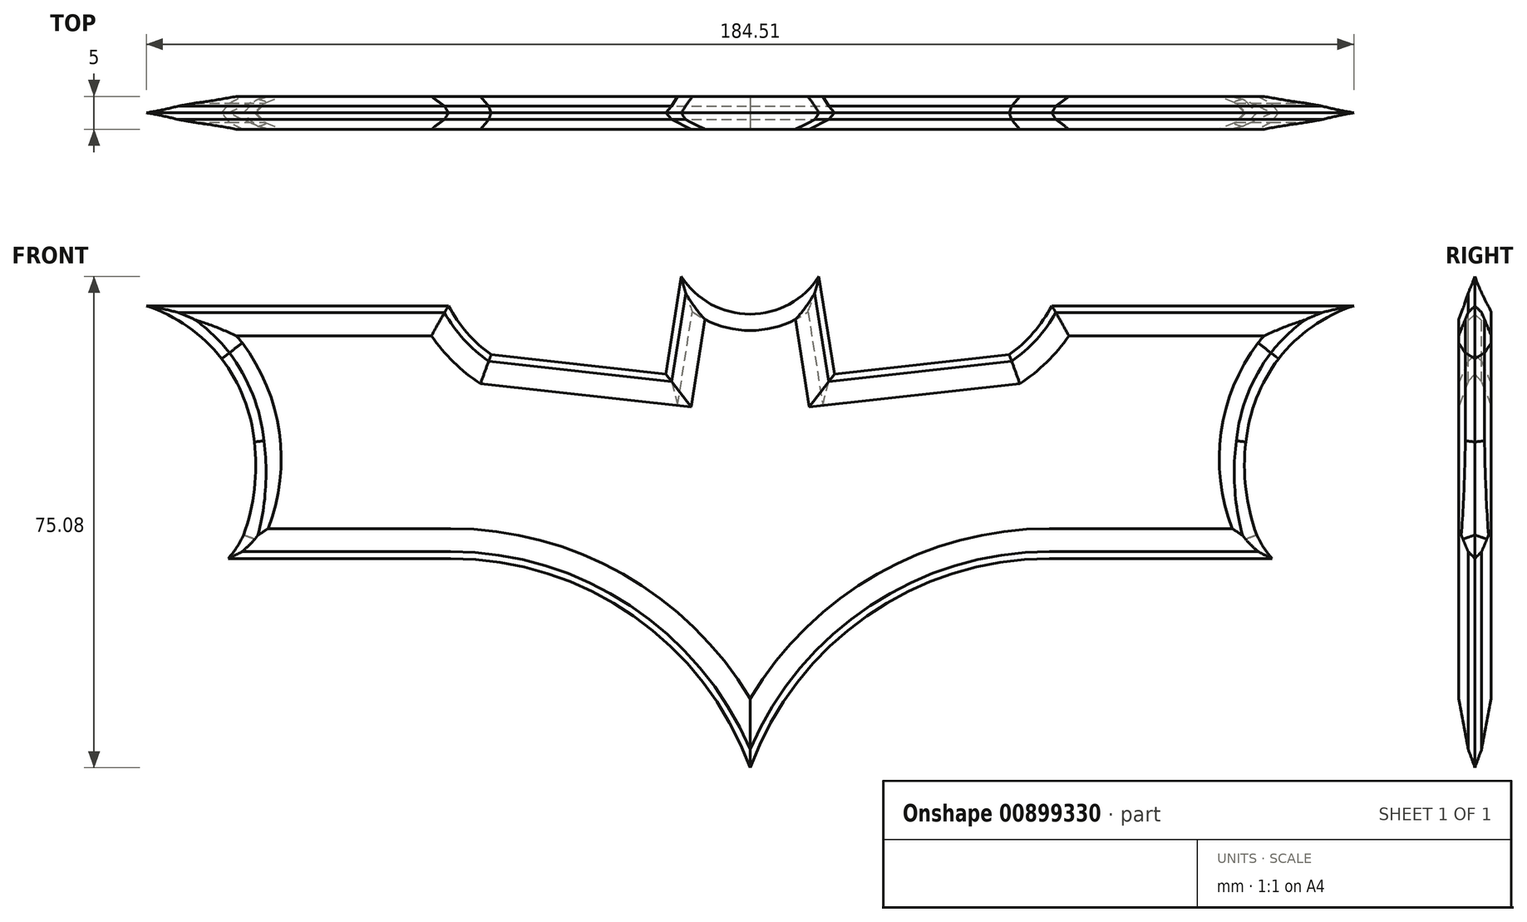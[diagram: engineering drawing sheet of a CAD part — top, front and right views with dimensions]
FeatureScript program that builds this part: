
annotation { "Feature Type Name" : "Feature", "Feature Type Description" : "" }
export const myFeature = defineFeature(function(context is Context, id is Id, definition is map)
    precondition{}
    {
        {
            var Q0;
            Q0=qCreatedBy(makeId("Front.planeOp"),FACE);
            var sketch = newSketch(context, id + "F0", { "sketchPlane" : qUnion([Q0])});
            skLineSegment(sketch, "E0", {"start": v(0, 0) * mm, "end": v(50, 0) * mm});
            skLineSegment(sketch, "E1", {"start": v(57, -8.48) * mm, "end": v(86.82, -11.78) * mm});
            skPoint(sketch, "E2", {"position": v(84.15, -2.31) * mm});
            skLineSegment(sketch, "E3", {"start": v(96.59, 0.22) * mm, "end": v(96.59, 7.53) * mm});
            skArc(sketch, "E4", {"start": v(86.82, 8.22) * mm, "mid": v(96.59, 0.22) * mm, "end": v(106.35, 8.22) * mm});
            skArc(sketch, "E5", {"start": v(96.59, -74.78) * mm, "mid": v(79.39, -50.1) * mm, "end": v(50.84, -40.6) * mm});
            skArc(sketch, "E6", {"start": v(15.84, -9.08) * mm, "mid": v(8.8, -3) * mm, "end": v(0, 0) * mm});
            skArc(sketch, "E7", {"start": v(20.83, -21.8) * mm, "mid": v(19.2, -15.1) * mm, "end": v(15.84, -9.08) * mm});
            skArc(sketch, "E8", {"start": v(19.17, -36.02) * mm, "mid": v(20.84, -29) * mm, "end": v(20.83, -21.8) * mm});
            skArc(sketch, "E9", {"start": v(15.84, -40.6) * mm, "mid": v(17.74, -38.48) * mm, "end": v(19.17, -36.02) * mm});
            skLineSegment(sketch, "E10", {"start": v(15.84, -40.6) * mm, "end": v(50.84, -40.6) * mm});
            skArc(sketch, "E11.MirrorCS", {"start": v(177.33, -9.08) * mm, "mid": v(184.37, -3) * mm, "end": v(193.17, 0) * mm});
            skArc(sketch, "E12.MirrorCS", {"start": v(172.34, -21.8) * mm, "mid": v(173.97, -15.1) * mm, "end": v(177.33, -9.08) * mm});
            skLineSegment(sketch, "E13.MirrorCS", {"start": v(193.17, 0) * mm, "end": v(143.17, 0) * mm});
            skLineSegment(sketch, "E14.MirrorCS", {"start": v(136.17, -8.48) * mm, "end": v(106.35, -11.78) * mm});
            skArc(sketch, "E15.MirrorCS", {"start": v(174, -36.02) * mm, "mid": v(172.33, -29) * mm, "end": v(172.34, -21.8) * mm});
            skArc(sketch, "E16.MirrorCS", {"start": v(177.33, -40.6) * mm, "mid": v(175.43, -38.48) * mm, "end": v(174, -36.02) * mm});
            skLineSegment(sketch, "E17.MirrorCS", {"start": v(177.33, -40.6) * mm, "end": v(142.33, -40.6) * mm});
            skArc(sketch, "E18.MirrorCS", {"start": v(96.59, -74.78) * mm, "mid": v(113.78, -50.1) * mm, "end": v(142.33, -40.6) * mm});
            skArc(sketch, "E19", {"start": v(50, 0) * mm, "mid": v(52.95, -4.7) * mm, "end": v(57, -8.48) * mm});
            skArc(sketch, "E20.MirrorCS", {"start": v(143.17, 0) * mm, "mid": v(140.23, -4.7) * mm, "end": v(136.17, -8.48) * mm});
            skLineSegment(sketch, "E21", {"start": v(86.82, 8.22) * mm, "end": v(83.72, -11.43) * mm});
            skLineSegment(sketch, "E22.MirrorCS", {"start": v(106.35, 8.22) * mm, "end": v(109.46, -11.43) * mm});
            skSolve(sketch);
        }
        {
            var Q0;
            Q0 = qSketchRegion(id + "F0", true);
            extrude(context, id + "F1", {"entities" : qUnion([Q0]), "depth" : 5 * mm, "offsetDistance" : 25 * mm});
        }
        {
            var Q0;
            Q0=makeQuery(id+"F1.opExtrude","CAP_EDGE",EDGE,{"disambiguationData":[OSD([sQuery(id+"F0.wireOp",EDGE,"E0")])],"isStart":false});
            var Q1;
            Q1=makeQuery(id+"F1.opExtrude","CAP_EDGE",EDGE,{"disambiguationData":[OSD([sQuery(id+"F0.wireOp",EDGE,"E0")])],"isStart":true});
            var Q2;
            Q2=makeQuery(id+"F1.opExtrude","CAP_EDGE",EDGE,{"disambiguationData":[OSD([sQuery(id+"F0.wireOp",EDGE,"E10")])],"isStart":false});
            var Q3;
            Q3=makeQuery(id+"F1.opExtrude","CAP_EDGE",EDGE,{"disambiguationData":[OSD([sQuery(id+"F0.wireOp",EDGE,"E10")])],"isStart":true});
            chamfer(context, id + "F2", {"entities" : qUnion([Q0, Q1, Q2, Q3]), "width" : 3.5 * mm, "tangentPropagation" : true});
        }
        {
            var Q0;
            Q0=makeQuery(id+"F1.opExtrude","CAP_EDGE",EDGE,{"disambiguationData":[OSD([sQuery(id+"F0.wireOp",EDGE,"E19")])],"isStart":false});
            var Q1;
            Q1=makeQuery(id+"F1.opExtrude","CAP_EDGE",EDGE,{"disambiguationData":[OSD([sQuery(id+"F0.wireOp",EDGE,"E19")])],"isStart":true});
            chamfer(context, id + "F3", {"entities" : qUnion([Q0, Q1]), "width" : 2.5 * mm, "tangentPropagation" : true});
        }
        {
            var Q0;
            Q0=makeQuery(id+"F1.opExtrude","CAP_EDGE",EDGE,{"disambiguationData":[OSD([sQuery(id+"F0.wireOp",EDGE,"E1")])],"isStart":false});
            var Q1;
            Q1=makeQuery(id+"F1.opExtrude","CAP_EDGE",EDGE,{"disambiguationData":[OSD([sQuery(id+"F0.wireOp",EDGE,"E1")])],"isStart":true});
            chamfer(context, id + "F4", {"entities" : qUnion([Q0, Q1]), "width" : 2.5 * mm, "tangentPropagation" : true});
        }
        {
            var Q0;
            Q0=makeQuery(id+"F1.opExtrude","CAP_EDGE",EDGE,{"disambiguationData":[OSD([sQuery(id+"F0.wireOp",EDGE,"E13.MirrorCS")])],"isStart":false});
            var Q1;
            Q1=makeQuery(id+"F1.opExtrude","CAP_EDGE",EDGE,{"disambiguationData":[OSD([sQuery(id+"F0.wireOp",EDGE,"E13.MirrorCS")])],"isStart":true});
            var Q2;
            Q2=makeQuery(id+"F1.opExtrude","CAP_EDGE",EDGE,{"disambiguationData":[OSD([sQuery(id+"F0.wireOp",EDGE,"E17.MirrorCS")])],"isStart":false});
            var Q3;
            Q3=makeQuery(id+"F1.opExtrude","CAP_EDGE",EDGE,{"disambiguationData":[OSD([sQuery(id+"F0.wireOp",EDGE,"E17.MirrorCS")])],"isStart":true});
            chamfer(context, id + "F5", {"entities" : qUnion([Q0, Q1, Q2, Q3]), "width" : 3.5 * mm, "tangentPropagation" : true});
        }
        {
            var Q0;
            Q0=makeQuery(id+"F1.opExtrude","CAP_EDGE",EDGE,{"disambiguationData":[OSD([sQuery(id+"F0.wireOp",EDGE,"E20.MirrorCS")])],"isStart":true});
            var Q1;
            Q1=makeQuery(id+"F1.opExtrude","CAP_EDGE",EDGE,{"disambiguationData":[OSD([sQuery(id+"F0.wireOp",EDGE,"E20.MirrorCS")])],"isStart":false});
            var Q2;
            Q2=makeQuery(id+"F1.opExtrude","CAP_EDGE",EDGE,{"disambiguationData":[OSD([sQuery(id+"F0.wireOp",EDGE,"E14.MirrorCS")])],"isStart":true});
            var Q3;
            Q3=makeQuery(id+"F1.opExtrude","CAP_EDGE",EDGE,{"disambiguationData":[OSD([sQuery(id+"F0.wireOp",EDGE,"E14.MirrorCS")])],"isStart":false});
            var Q4;
            Q4=makeQuery(id+"F1.opExtrude","CAP_EDGE",EDGE,{"disambiguationData":[OSD([sQuery(id+"F0.wireOp",EDGE,"E22.MirrorCS")])],"isStart":true});
            var Q5;
            Q5=makeQuery(id+"F1.opExtrude","CAP_EDGE",EDGE,{"disambiguationData":[OSD([sQuery(id+"F0.wireOp",EDGE,"E22.MirrorCS")])],"isStart":false});
            var Q6;
            Q6=makeQuery(id+"F1.opExtrude","CAP_EDGE",EDGE,{"disambiguationData":[OSD([sQuery(id+"F0.wireOp",EDGE,"E21")])],"isStart":true});
            var Q7;
            Q7=makeQuery(id+"F1.opExtrude","CAP_EDGE",EDGE,{"disambiguationData":[OSD([sQuery(id+"F0.wireOp",EDGE,"E21")])],"isStart":false});
            chamfer(context, id + "F6", {"entities" : qUnion([Q0, Q1, Q2, Q3, Q4, Q5, Q6, Q7]), "width" : 2.5 * mm, "tangentPropagation" : true});
        }
        {
            var Q0;
            Q0=makeQuery(id+"F1.opExtrude","CAP_EDGE",EDGE,{"disambiguationData":[OSD([sQuery(id+"F0.wireOp",EDGE,"E4")])],"isStart":true});
            var Q1;
            Q1=makeQuery(id+"F1.opExtrude","CAP_EDGE",EDGE,{"disambiguationData":[OSD([sQuery(id+"F0.wireOp",EDGE,"E4")])],"isStart":false});
            chamfer(context, id + "F7", {"entities" : qUnion([Q0, Q1]), "width" : 5 * mm, "tangentPropagation" : true});
        }
        {
            var Q0;
            {var subQ0=sQuery(id+"F0.wireOp",EDGE,"E13.MirrorCS");Q0=makeQuery(id+"F5.opChamfer","BLEND_EDGE",EDGE,{"blendedFrom":[makeQuery(id+"F1.opExtrude","CAP_EDGE",EDGE,{"disambiguationData":[OSD([subQ0])],"isStart":true}),makeQuery(id+"F1.opExtrude","CAP_FACE",FACE,{"disambiguationData":[OSD([sQuery(id+"F0.wireOp",EDGE,"E0"),sQuery(id+"F0.wireOp",EDGE,"E1"),sQuery(id+"F0.wireOp",EDGE,"E4"),sQuery(id+"F0.wireOp",EDGE,"E5"),sQuery(id+"F0.wireOp",EDGE,"E6"),sQuery(id+"F0.wireOp",EDGE,"E7"),sQuery(id+"F0.wireOp",EDGE,"E8"),sQuery(id+"F0.wireOp",EDGE,"E9"),sQuery(id+"F0.wireOp",EDGE,"E10"),sQuery(id+"F0.wireOp",EDGE,"E11.MirrorCS"),sQuery(id+"F0.wireOp",EDGE,"E12.MirrorCS"),subQ0,sQuery(id+"F0.wireOp",EDGE,"E14.MirrorCS"),sQuery(id+"F0.wireOp",EDGE,"E15.MirrorCS"),sQuery(id+"F0.wireOp",EDGE,"E16.MirrorCS"),sQuery(id+"F0.wireOp",EDGE,"E17.MirrorCS"),sQuery(id+"F0.wireOp",EDGE,"E18.MirrorCS"),sQuery(id+"F0.wireOp",EDGE,"E19"),sQuery(id+"F0.wireOp",EDGE,"E20.MirrorCS"),sQuery(id+"F0.wireOp",EDGE,"E21"),sQuery(id+"F0.wireOp",EDGE,"E22.MirrorCS")])],"isStart":true})],"blendedInto":[makeQuery(id+"F1.opExtrude","CAP_FACE",FACE,{"disambiguationData":[OSD([sQuery(id+"F0.wireOp",EDGE,"E0"),sQuery(id+"F0.wireOp",EDGE,"E1"),sQuery(id+"F0.wireOp",EDGE,"E4"),sQuery(id+"F0.wireOp",EDGE,"E5"),sQuery(id+"F0.wireOp",EDGE,"E6"),sQuery(id+"F0.wireOp",EDGE,"E7"),sQuery(id+"F0.wireOp",EDGE,"E8"),sQuery(id+"F0.wireOp",EDGE,"E9"),sQuery(id+"F0.wireOp",EDGE,"E10"),sQuery(id+"F0.wireOp",EDGE,"E11.MirrorCS"),sQuery(id+"F0.wireOp",EDGE,"E12.MirrorCS"),subQ0,sQuery(id+"F0.wireOp",EDGE,"E14.MirrorCS"),sQuery(id+"F0.wireOp",EDGE,"E15.MirrorCS"),sQuery(id+"F0.wireOp",EDGE,"E16.MirrorCS"),sQuery(id+"F0.wireOp",EDGE,"E17.MirrorCS"),sQuery(id+"F0.wireOp",EDGE,"E18.MirrorCS"),sQuery(id+"F0.wireOp",EDGE,"E19"),sQuery(id+"F0.wireOp",EDGE,"E20.MirrorCS"),sQuery(id+"F0.wireOp",EDGE,"E21"),sQuery(id+"F0.wireOp",EDGE,"E22.MirrorCS")])],"isStart":true})]});}
            var Q1;
            {var subQ0=sQuery(id+"F0.wireOp",EDGE,"E12.MirrorCS");Q1=makeQuery(id+"F5.opChamfer","BLEND_EDGE",EDGE,{"blendedFrom":[makeQuery(id+"F1.opExtrude","CAP_EDGE",EDGE,{"disambiguationData":[OSD([subQ0])],"isStart":true}),makeQuery(id+"F1.opExtrude","CAP_FACE",FACE,{"disambiguationData":[OSD([sQuery(id+"F0.wireOp",EDGE,"E0"),sQuery(id+"F0.wireOp",EDGE,"E1"),sQuery(id+"F0.wireOp",EDGE,"E4"),sQuery(id+"F0.wireOp",EDGE,"E5"),sQuery(id+"F0.wireOp",EDGE,"E6"),sQuery(id+"F0.wireOp",EDGE,"E7"),sQuery(id+"F0.wireOp",EDGE,"E8"),sQuery(id+"F0.wireOp",EDGE,"E9"),sQuery(id+"F0.wireOp",EDGE,"E10"),sQuery(id+"F0.wireOp",EDGE,"E11.MirrorCS"),subQ0,sQuery(id+"F0.wireOp",EDGE,"E13.MirrorCS"),sQuery(id+"F0.wireOp",EDGE,"E14.MirrorCS"),sQuery(id+"F0.wireOp",EDGE,"E15.MirrorCS"),sQuery(id+"F0.wireOp",EDGE,"E16.MirrorCS"),sQuery(id+"F0.wireOp",EDGE,"E17.MirrorCS"),sQuery(id+"F0.wireOp",EDGE,"E18.MirrorCS"),sQuery(id+"F0.wireOp",EDGE,"E19"),sQuery(id+"F0.wireOp",EDGE,"E20.MirrorCS"),sQuery(id+"F0.wireOp",EDGE,"E21"),sQuery(id+"F0.wireOp",EDGE,"E22.MirrorCS")])],"isStart":true})],"blendedInto":[makeQuery(id+"F1.opExtrude","CAP_FACE",FACE,{"disambiguationData":[OSD([sQuery(id+"F0.wireOp",EDGE,"E0"),sQuery(id+"F0.wireOp",EDGE,"E1"),sQuery(id+"F0.wireOp",EDGE,"E4"),sQuery(id+"F0.wireOp",EDGE,"E5"),sQuery(id+"F0.wireOp",EDGE,"E6"),sQuery(id+"F0.wireOp",EDGE,"E7"),sQuery(id+"F0.wireOp",EDGE,"E8"),sQuery(id+"F0.wireOp",EDGE,"E9"),sQuery(id+"F0.wireOp",EDGE,"E10"),sQuery(id+"F0.wireOp",EDGE,"E11.MirrorCS"),subQ0,sQuery(id+"F0.wireOp",EDGE,"E13.MirrorCS"),sQuery(id+"F0.wireOp",EDGE,"E14.MirrorCS"),sQuery(id+"F0.wireOp",EDGE,"E15.MirrorCS"),sQuery(id+"F0.wireOp",EDGE,"E16.MirrorCS"),sQuery(id+"F0.wireOp",EDGE,"E17.MirrorCS"),sQuery(id+"F0.wireOp",EDGE,"E18.MirrorCS"),sQuery(id+"F0.wireOp",EDGE,"E19"),sQuery(id+"F0.wireOp",EDGE,"E20.MirrorCS"),sQuery(id+"F0.wireOp",EDGE,"E21"),sQuery(id+"F0.wireOp",EDGE,"E22.MirrorCS")])],"isStart":true})]});}
            var Q2;
            {var subQ0=sQuery(id+"F0.wireOp",EDGE,"E14.MirrorCS");Q2=makeQuery(id+"F6.opChamfer","BLEND_EDGE",EDGE,{"blendedFrom":[makeQuery(id+"F1.opExtrude","CAP_EDGE",EDGE,{"disambiguationData":[OSD([subQ0])],"isStart":true}),makeQuery(id+"F1.opExtrude","CAP_FACE",FACE,{"disambiguationData":[OSD([sQuery(id+"F0.wireOp",EDGE,"E0"),sQuery(id+"F0.wireOp",EDGE,"E1"),sQuery(id+"F0.wireOp",EDGE,"E4"),sQuery(id+"F0.wireOp",EDGE,"E5"),sQuery(id+"F0.wireOp",EDGE,"E6"),sQuery(id+"F0.wireOp",EDGE,"E7"),sQuery(id+"F0.wireOp",EDGE,"E8"),sQuery(id+"F0.wireOp",EDGE,"E9"),sQuery(id+"F0.wireOp",EDGE,"E10"),sQuery(id+"F0.wireOp",EDGE,"E11.MirrorCS"),sQuery(id+"F0.wireOp",EDGE,"E12.MirrorCS"),sQuery(id+"F0.wireOp",EDGE,"E13.MirrorCS"),subQ0,sQuery(id+"F0.wireOp",EDGE,"E15.MirrorCS"),sQuery(id+"F0.wireOp",EDGE,"E16.MirrorCS"),sQuery(id+"F0.wireOp",EDGE,"E17.MirrorCS"),sQuery(id+"F0.wireOp",EDGE,"E18.MirrorCS"),sQuery(id+"F0.wireOp",EDGE,"E19"),sQuery(id+"F0.wireOp",EDGE,"E20.MirrorCS"),sQuery(id+"F0.wireOp",EDGE,"E21"),sQuery(id+"F0.wireOp",EDGE,"E22.MirrorCS")])],"isStart":true})],"blendedInto":[makeQuery(id+"F1.opExtrude","CAP_FACE",FACE,{"disambiguationData":[OSD([sQuery(id+"F0.wireOp",EDGE,"E0"),sQuery(id+"F0.wireOp",EDGE,"E1"),sQuery(id+"F0.wireOp",EDGE,"E4"),sQuery(id+"F0.wireOp",EDGE,"E5"),sQuery(id+"F0.wireOp",EDGE,"E6"),sQuery(id+"F0.wireOp",EDGE,"E7"),sQuery(id+"F0.wireOp",EDGE,"E8"),sQuery(id+"F0.wireOp",EDGE,"E9"),sQuery(id+"F0.wireOp",EDGE,"E10"),sQuery(id+"F0.wireOp",EDGE,"E11.MirrorCS"),sQuery(id+"F0.wireOp",EDGE,"E12.MirrorCS"),sQuery(id+"F0.wireOp",EDGE,"E13.MirrorCS"),subQ0,sQuery(id+"F0.wireOp",EDGE,"E15.MirrorCS"),sQuery(id+"F0.wireOp",EDGE,"E16.MirrorCS"),sQuery(id+"F0.wireOp",EDGE,"E17.MirrorCS"),sQuery(id+"F0.wireOp",EDGE,"E18.MirrorCS"),sQuery(id+"F0.wireOp",EDGE,"E19"),sQuery(id+"F0.wireOp",EDGE,"E20.MirrorCS"),sQuery(id+"F0.wireOp",EDGE,"E21"),sQuery(id+"F0.wireOp",EDGE,"E22.MirrorCS")])],"isStart":true})]});}
            var Q3;
            {var subQ0=sQuery(id+"F0.wireOp",EDGE,"E17.MirrorCS");Q3=makeQuery(id+"F5.opChamfer","BLEND_EDGE",EDGE,{"blendedFrom":[makeQuery(id+"F1.opExtrude","CAP_EDGE",EDGE,{"disambiguationData":[OSD([subQ0])],"isStart":true}),makeQuery(id+"F1.opExtrude","CAP_FACE",FACE,{"disambiguationData":[OSD([sQuery(id+"F0.wireOp",EDGE,"E0"),sQuery(id+"F0.wireOp",EDGE,"E1"),sQuery(id+"F0.wireOp",EDGE,"E4"),sQuery(id+"F0.wireOp",EDGE,"E5"),sQuery(id+"F0.wireOp",EDGE,"E6"),sQuery(id+"F0.wireOp",EDGE,"E7"),sQuery(id+"F0.wireOp",EDGE,"E8"),sQuery(id+"F0.wireOp",EDGE,"E9"),sQuery(id+"F0.wireOp",EDGE,"E10"),sQuery(id+"F0.wireOp",EDGE,"E11.MirrorCS"),sQuery(id+"F0.wireOp",EDGE,"E12.MirrorCS"),sQuery(id+"F0.wireOp",EDGE,"E13.MirrorCS"),sQuery(id+"F0.wireOp",EDGE,"E14.MirrorCS"),sQuery(id+"F0.wireOp",EDGE,"E15.MirrorCS"),sQuery(id+"F0.wireOp",EDGE,"E16.MirrorCS"),subQ0,sQuery(id+"F0.wireOp",EDGE,"E18.MirrorCS"),sQuery(id+"F0.wireOp",EDGE,"E19"),sQuery(id+"F0.wireOp",EDGE,"E20.MirrorCS"),sQuery(id+"F0.wireOp",EDGE,"E21"),sQuery(id+"F0.wireOp",EDGE,"E22.MirrorCS")])],"isStart":true})],"blendedInto":[makeQuery(id+"F1.opExtrude","CAP_FACE",FACE,{"disambiguationData":[OSD([sQuery(id+"F0.wireOp",EDGE,"E0"),sQuery(id+"F0.wireOp",EDGE,"E1"),sQuery(id+"F0.wireOp",EDGE,"E4"),sQuery(id+"F0.wireOp",EDGE,"E5"),sQuery(id+"F0.wireOp",EDGE,"E6"),sQuery(id+"F0.wireOp",EDGE,"E7"),sQuery(id+"F0.wireOp",EDGE,"E8"),sQuery(id+"F0.wireOp",EDGE,"E9"),sQuery(id+"F0.wireOp",EDGE,"E10"),sQuery(id+"F0.wireOp",EDGE,"E11.MirrorCS"),sQuery(id+"F0.wireOp",EDGE,"E12.MirrorCS"),sQuery(id+"F0.wireOp",EDGE,"E13.MirrorCS"),sQuery(id+"F0.wireOp",EDGE,"E14.MirrorCS"),sQuery(id+"F0.wireOp",EDGE,"E15.MirrorCS"),sQuery(id+"F0.wireOp",EDGE,"E16.MirrorCS"),subQ0,sQuery(id+"F0.wireOp",EDGE,"E18.MirrorCS"),sQuery(id+"F0.wireOp",EDGE,"E19"),sQuery(id+"F0.wireOp",EDGE,"E20.MirrorCS"),sQuery(id+"F0.wireOp",EDGE,"E21"),sQuery(id+"F0.wireOp",EDGE,"E22.MirrorCS")])],"isStart":true})]});}
            var Q4;
            {var subQ0=sQuery(id+"F0.wireOp",EDGE,"E1");Q4=makeQuery(id+"F4.opChamfer","BLEND_EDGE",EDGE,{"blendedFrom":[makeQuery(id+"F1.opExtrude","CAP_EDGE",EDGE,{"disambiguationData":[OSD([subQ0])],"isStart":true}),makeQuery(id+"F1.opExtrude","CAP_FACE",FACE,{"disambiguationData":[OSD([sQuery(id+"F0.wireOp",EDGE,"E0"),subQ0,sQuery(id+"F0.wireOp",EDGE,"E4"),sQuery(id+"F0.wireOp",EDGE,"E5"),sQuery(id+"F0.wireOp",EDGE,"E6"),sQuery(id+"F0.wireOp",EDGE,"E7"),sQuery(id+"F0.wireOp",EDGE,"E8"),sQuery(id+"F0.wireOp",EDGE,"E9"),sQuery(id+"F0.wireOp",EDGE,"E10"),sQuery(id+"F0.wireOp",EDGE,"E11.MirrorCS"),sQuery(id+"F0.wireOp",EDGE,"E12.MirrorCS"),sQuery(id+"F0.wireOp",EDGE,"E13.MirrorCS"),sQuery(id+"F0.wireOp",EDGE,"E14.MirrorCS"),sQuery(id+"F0.wireOp",EDGE,"E15.MirrorCS"),sQuery(id+"F0.wireOp",EDGE,"E16.MirrorCS"),sQuery(id+"F0.wireOp",EDGE,"E17.MirrorCS"),sQuery(id+"F0.wireOp",EDGE,"E18.MirrorCS"),sQuery(id+"F0.wireOp",EDGE,"E19"),sQuery(id+"F0.wireOp",EDGE,"E20.MirrorCS"),sQuery(id+"F0.wireOp",EDGE,"E21"),sQuery(id+"F0.wireOp",EDGE,"E22.MirrorCS")])],"isStart":true})],"blendedInto":[makeQuery(id+"F1.opExtrude","CAP_FACE",FACE,{"disambiguationData":[OSD([sQuery(id+"F0.wireOp",EDGE,"E0"),subQ0,sQuery(id+"F0.wireOp",EDGE,"E4"),sQuery(id+"F0.wireOp",EDGE,"E5"),sQuery(id+"F0.wireOp",EDGE,"E6"),sQuery(id+"F0.wireOp",EDGE,"E7"),sQuery(id+"F0.wireOp",EDGE,"E8"),sQuery(id+"F0.wireOp",EDGE,"E9"),sQuery(id+"F0.wireOp",EDGE,"E10"),sQuery(id+"F0.wireOp",EDGE,"E11.MirrorCS"),sQuery(id+"F0.wireOp",EDGE,"E12.MirrorCS"),sQuery(id+"F0.wireOp",EDGE,"E13.MirrorCS"),sQuery(id+"F0.wireOp",EDGE,"E14.MirrorCS"),sQuery(id+"F0.wireOp",EDGE,"E15.MirrorCS"),sQuery(id+"F0.wireOp",EDGE,"E16.MirrorCS"),sQuery(id+"F0.wireOp",EDGE,"E17.MirrorCS"),sQuery(id+"F0.wireOp",EDGE,"E18.MirrorCS"),sQuery(id+"F0.wireOp",EDGE,"E19"),sQuery(id+"F0.wireOp",EDGE,"E20.MirrorCS"),sQuery(id+"F0.wireOp",EDGE,"E21"),sQuery(id+"F0.wireOp",EDGE,"E22.MirrorCS")])],"isStart":true})]});}
            var Q5;
            {var subQ0=sQuery(id+"F0.wireOp",EDGE,"E0");Q5=makeQuery(id+"F2.opChamfer","BLEND_EDGE",EDGE,{"blendedFrom":[makeQuery(id+"F1.opExtrude","CAP_EDGE",EDGE,{"disambiguationData":[OSD([subQ0])],"isStart":true}),makeQuery(id+"F1.opExtrude","CAP_FACE",FACE,{"disambiguationData":[OSD([subQ0,sQuery(id+"F0.wireOp",EDGE,"E1"),sQuery(id+"F0.wireOp",EDGE,"E4"),sQuery(id+"F0.wireOp",EDGE,"E5"),sQuery(id+"F0.wireOp",EDGE,"E6"),sQuery(id+"F0.wireOp",EDGE,"E7"),sQuery(id+"F0.wireOp",EDGE,"E8"),sQuery(id+"F0.wireOp",EDGE,"E9"),sQuery(id+"F0.wireOp",EDGE,"E10"),sQuery(id+"F0.wireOp",EDGE,"E11.MirrorCS"),sQuery(id+"F0.wireOp",EDGE,"E12.MirrorCS"),sQuery(id+"F0.wireOp",EDGE,"E13.MirrorCS"),sQuery(id+"F0.wireOp",EDGE,"E14.MirrorCS"),sQuery(id+"F0.wireOp",EDGE,"E15.MirrorCS"),sQuery(id+"F0.wireOp",EDGE,"E16.MirrorCS"),sQuery(id+"F0.wireOp",EDGE,"E17.MirrorCS"),sQuery(id+"F0.wireOp",EDGE,"E18.MirrorCS"),sQuery(id+"F0.wireOp",EDGE,"E19"),sQuery(id+"F0.wireOp",EDGE,"E20.MirrorCS"),sQuery(id+"F0.wireOp",EDGE,"E21"),sQuery(id+"F0.wireOp",EDGE,"E22.MirrorCS")])],"isStart":true})],"blendedInto":[makeQuery(id+"F1.opExtrude","CAP_FACE",FACE,{"disambiguationData":[OSD([subQ0,sQuery(id+"F0.wireOp",EDGE,"E1"),sQuery(id+"F0.wireOp",EDGE,"E4"),sQuery(id+"F0.wireOp",EDGE,"E5"),sQuery(id+"F0.wireOp",EDGE,"E6"),sQuery(id+"F0.wireOp",EDGE,"E7"),sQuery(id+"F0.wireOp",EDGE,"E8"),sQuery(id+"F0.wireOp",EDGE,"E9"),sQuery(id+"F0.wireOp",EDGE,"E10"),sQuery(id+"F0.wireOp",EDGE,"E11.MirrorCS"),sQuery(id+"F0.wireOp",EDGE,"E12.MirrorCS"),sQuery(id+"F0.wireOp",EDGE,"E13.MirrorCS"),sQuery(id+"F0.wireOp",EDGE,"E14.MirrorCS"),sQuery(id+"F0.wireOp",EDGE,"E15.MirrorCS"),sQuery(id+"F0.wireOp",EDGE,"E16.MirrorCS"),sQuery(id+"F0.wireOp",EDGE,"E17.MirrorCS"),sQuery(id+"F0.wireOp",EDGE,"E18.MirrorCS"),sQuery(id+"F0.wireOp",EDGE,"E19"),sQuery(id+"F0.wireOp",EDGE,"E20.MirrorCS"),sQuery(id+"F0.wireOp",EDGE,"E21"),sQuery(id+"F0.wireOp",EDGE,"E22.MirrorCS")])],"isStart":true})]});}
            var Q6;
            {var subQ0=sQuery(id+"F0.wireOp",EDGE,"E20.MirrorCS");Q6=makeQuery(id+"F6.opChamfer","BLEND_EDGE",EDGE,{"blendedFrom":[makeQuery(id+"F1.opExtrude","CAP_EDGE",EDGE,{"disambiguationData":[OSD([subQ0])],"isStart":true}),makeQuery(id+"F1.opExtrude","CAP_FACE",FACE,{"disambiguationData":[OSD([sQuery(id+"F0.wireOp",EDGE,"E0"),sQuery(id+"F0.wireOp",EDGE,"E1"),sQuery(id+"F0.wireOp",EDGE,"E4"),sQuery(id+"F0.wireOp",EDGE,"E5"),sQuery(id+"F0.wireOp",EDGE,"E6"),sQuery(id+"F0.wireOp",EDGE,"E7"),sQuery(id+"F0.wireOp",EDGE,"E8"),sQuery(id+"F0.wireOp",EDGE,"E9"),sQuery(id+"F0.wireOp",EDGE,"E10"),sQuery(id+"F0.wireOp",EDGE,"E11.MirrorCS"),sQuery(id+"F0.wireOp",EDGE,"E12.MirrorCS"),sQuery(id+"F0.wireOp",EDGE,"E13.MirrorCS"),sQuery(id+"F0.wireOp",EDGE,"E14.MirrorCS"),sQuery(id+"F0.wireOp",EDGE,"E15.MirrorCS"),sQuery(id+"F0.wireOp",EDGE,"E16.MirrorCS"),sQuery(id+"F0.wireOp",EDGE,"E17.MirrorCS"),sQuery(id+"F0.wireOp",EDGE,"E18.MirrorCS"),sQuery(id+"F0.wireOp",EDGE,"E19"),subQ0,sQuery(id+"F0.wireOp",EDGE,"E21"),sQuery(id+"F0.wireOp",EDGE,"E22.MirrorCS")])],"isStart":true})],"blendedInto":[makeQuery(id+"F1.opExtrude","CAP_FACE",FACE,{"disambiguationData":[OSD([sQuery(id+"F0.wireOp",EDGE,"E0"),sQuery(id+"F0.wireOp",EDGE,"E1"),sQuery(id+"F0.wireOp",EDGE,"E4"),sQuery(id+"F0.wireOp",EDGE,"E5"),sQuery(id+"F0.wireOp",EDGE,"E6"),sQuery(id+"F0.wireOp",EDGE,"E7"),sQuery(id+"F0.wireOp",EDGE,"E8"),sQuery(id+"F0.wireOp",EDGE,"E9"),sQuery(id+"F0.wireOp",EDGE,"E10"),sQuery(id+"F0.wireOp",EDGE,"E11.MirrorCS"),sQuery(id+"F0.wireOp",EDGE,"E12.MirrorCS"),sQuery(id+"F0.wireOp",EDGE,"E13.MirrorCS"),sQuery(id+"F0.wireOp",EDGE,"E14.MirrorCS"),sQuery(id+"F0.wireOp",EDGE,"E15.MirrorCS"),sQuery(id+"F0.wireOp",EDGE,"E16.MirrorCS"),sQuery(id+"F0.wireOp",EDGE,"E17.MirrorCS"),sQuery(id+"F0.wireOp",EDGE,"E18.MirrorCS"),sQuery(id+"F0.wireOp",EDGE,"E19"),subQ0,sQuery(id+"F0.wireOp",EDGE,"E21"),sQuery(id+"F0.wireOp",EDGE,"E22.MirrorCS")])],"isStart":true})]});}
            var Q7;
            {var subQ0=sQuery(id+"F0.wireOp",EDGE,"E19");Q7=makeQuery(id+"F3.opChamfer","BLEND_EDGE",EDGE,{"blendedFrom":[makeQuery(id+"F1.opExtrude","CAP_EDGE",EDGE,{"disambiguationData":[OSD([subQ0])],"isStart":true}),makeQuery(id+"F1.opExtrude","CAP_FACE",FACE,{"disambiguationData":[OSD([sQuery(id+"F0.wireOp",EDGE,"E0"),sQuery(id+"F0.wireOp",EDGE,"E1"),sQuery(id+"F0.wireOp",EDGE,"E4"),sQuery(id+"F0.wireOp",EDGE,"E5"),sQuery(id+"F0.wireOp",EDGE,"E6"),sQuery(id+"F0.wireOp",EDGE,"E7"),sQuery(id+"F0.wireOp",EDGE,"E8"),sQuery(id+"F0.wireOp",EDGE,"E9"),sQuery(id+"F0.wireOp",EDGE,"E10"),sQuery(id+"F0.wireOp",EDGE,"E11.MirrorCS"),sQuery(id+"F0.wireOp",EDGE,"E12.MirrorCS"),sQuery(id+"F0.wireOp",EDGE,"E13.MirrorCS"),sQuery(id+"F0.wireOp",EDGE,"E14.MirrorCS"),sQuery(id+"F0.wireOp",EDGE,"E15.MirrorCS"),sQuery(id+"F0.wireOp",EDGE,"E16.MirrorCS"),sQuery(id+"F0.wireOp",EDGE,"E17.MirrorCS"),sQuery(id+"F0.wireOp",EDGE,"E18.MirrorCS"),subQ0,sQuery(id+"F0.wireOp",EDGE,"E20.MirrorCS"),sQuery(id+"F0.wireOp",EDGE,"E21"),sQuery(id+"F0.wireOp",EDGE,"E22.MirrorCS")])],"isStart":true})],"blendedInto":[makeQuery(id+"F1.opExtrude","CAP_FACE",FACE,{"disambiguationData":[OSD([sQuery(id+"F0.wireOp",EDGE,"E0"),sQuery(id+"F0.wireOp",EDGE,"E1"),sQuery(id+"F0.wireOp",EDGE,"E4"),sQuery(id+"F0.wireOp",EDGE,"E5"),sQuery(id+"F0.wireOp",EDGE,"E6"),sQuery(id+"F0.wireOp",EDGE,"E7"),sQuery(id+"F0.wireOp",EDGE,"E8"),sQuery(id+"F0.wireOp",EDGE,"E9"),sQuery(id+"F0.wireOp",EDGE,"E10"),sQuery(id+"F0.wireOp",EDGE,"E11.MirrorCS"),sQuery(id+"F0.wireOp",EDGE,"E12.MirrorCS"),sQuery(id+"F0.wireOp",EDGE,"E13.MirrorCS"),sQuery(id+"F0.wireOp",EDGE,"E14.MirrorCS"),sQuery(id+"F0.wireOp",EDGE,"E15.MirrorCS"),sQuery(id+"F0.wireOp",EDGE,"E16.MirrorCS"),sQuery(id+"F0.wireOp",EDGE,"E17.MirrorCS"),sQuery(id+"F0.wireOp",EDGE,"E18.MirrorCS"),subQ0,sQuery(id+"F0.wireOp",EDGE,"E20.MirrorCS"),sQuery(id+"F0.wireOp",EDGE,"E21"),sQuery(id+"F0.wireOp",EDGE,"E22.MirrorCS")])],"isStart":true})]});}
            var Q8;
            {var subQ0=sQuery(id+"F0.wireOp",EDGE,"E7");Q8=makeQuery(id+"F2.opChamfer","BLEND_EDGE",EDGE,{"blendedFrom":[makeQuery(id+"F1.opExtrude","CAP_EDGE",EDGE,{"disambiguationData":[OSD([subQ0])],"isStart":true}),makeQuery(id+"F1.opExtrude","CAP_FACE",FACE,{"disambiguationData":[OSD([sQuery(id+"F0.wireOp",EDGE,"E0"),sQuery(id+"F0.wireOp",EDGE,"E1"),sQuery(id+"F0.wireOp",EDGE,"E4"),sQuery(id+"F0.wireOp",EDGE,"E5"),sQuery(id+"F0.wireOp",EDGE,"E6"),subQ0,sQuery(id+"F0.wireOp",EDGE,"E8"),sQuery(id+"F0.wireOp",EDGE,"E9"),sQuery(id+"F0.wireOp",EDGE,"E10"),sQuery(id+"F0.wireOp",EDGE,"E11.MirrorCS"),sQuery(id+"F0.wireOp",EDGE,"E12.MirrorCS"),sQuery(id+"F0.wireOp",EDGE,"E13.MirrorCS"),sQuery(id+"F0.wireOp",EDGE,"E14.MirrorCS"),sQuery(id+"F0.wireOp",EDGE,"E15.MirrorCS"),sQuery(id+"F0.wireOp",EDGE,"E16.MirrorCS"),sQuery(id+"F0.wireOp",EDGE,"E17.MirrorCS"),sQuery(id+"F0.wireOp",EDGE,"E18.MirrorCS"),sQuery(id+"F0.wireOp",EDGE,"E19"),sQuery(id+"F0.wireOp",EDGE,"E20.MirrorCS"),sQuery(id+"F0.wireOp",EDGE,"E21"),sQuery(id+"F0.wireOp",EDGE,"E22.MirrorCS")])],"isStart":true})],"blendedInto":[makeQuery(id+"F1.opExtrude","CAP_FACE",FACE,{"disambiguationData":[OSD([sQuery(id+"F0.wireOp",EDGE,"E0"),sQuery(id+"F0.wireOp",EDGE,"E1"),sQuery(id+"F0.wireOp",EDGE,"E4"),sQuery(id+"F0.wireOp",EDGE,"E5"),sQuery(id+"F0.wireOp",EDGE,"E6"),subQ0,sQuery(id+"F0.wireOp",EDGE,"E8"),sQuery(id+"F0.wireOp",EDGE,"E9"),sQuery(id+"F0.wireOp",EDGE,"E10"),sQuery(id+"F0.wireOp",EDGE,"E11.MirrorCS"),sQuery(id+"F0.wireOp",EDGE,"E12.MirrorCS"),sQuery(id+"F0.wireOp",EDGE,"E13.MirrorCS"),sQuery(id+"F0.wireOp",EDGE,"E14.MirrorCS"),sQuery(id+"F0.wireOp",EDGE,"E15.MirrorCS"),sQuery(id+"F0.wireOp",EDGE,"E16.MirrorCS"),sQuery(id+"F0.wireOp",EDGE,"E17.MirrorCS"),sQuery(id+"F0.wireOp",EDGE,"E18.MirrorCS"),sQuery(id+"F0.wireOp",EDGE,"E19"),sQuery(id+"F0.wireOp",EDGE,"E20.MirrorCS"),sQuery(id+"F0.wireOp",EDGE,"E21"),sQuery(id+"F0.wireOp",EDGE,"E22.MirrorCS")])],"isStart":true})]});}
            var Q9;
            {var subQ0=sQuery(id+"F0.wireOp",EDGE,"E10");Q9=makeQuery(id+"F2.opChamfer","BLEND_EDGE",EDGE,{"blendedFrom":[makeQuery(id+"F1.opExtrude","CAP_EDGE",EDGE,{"disambiguationData":[OSD([subQ0])],"isStart":true}),makeQuery(id+"F1.opExtrude","CAP_FACE",FACE,{"disambiguationData":[OSD([sQuery(id+"F0.wireOp",EDGE,"E0"),sQuery(id+"F0.wireOp",EDGE,"E1"),sQuery(id+"F0.wireOp",EDGE,"E4"),sQuery(id+"F0.wireOp",EDGE,"E5"),sQuery(id+"F0.wireOp",EDGE,"E6"),sQuery(id+"F0.wireOp",EDGE,"E7"),sQuery(id+"F0.wireOp",EDGE,"E8"),sQuery(id+"F0.wireOp",EDGE,"E9"),subQ0,sQuery(id+"F0.wireOp",EDGE,"E11.MirrorCS"),sQuery(id+"F0.wireOp",EDGE,"E12.MirrorCS"),sQuery(id+"F0.wireOp",EDGE,"E13.MirrorCS"),sQuery(id+"F0.wireOp",EDGE,"E14.MirrorCS"),sQuery(id+"F0.wireOp",EDGE,"E15.MirrorCS"),sQuery(id+"F0.wireOp",EDGE,"E16.MirrorCS"),sQuery(id+"F0.wireOp",EDGE,"E17.MirrorCS"),sQuery(id+"F0.wireOp",EDGE,"E18.MirrorCS"),sQuery(id+"F0.wireOp",EDGE,"E19"),sQuery(id+"F0.wireOp",EDGE,"E20.MirrorCS"),sQuery(id+"F0.wireOp",EDGE,"E21"),sQuery(id+"F0.wireOp",EDGE,"E22.MirrorCS")])],"isStart":true})],"blendedInto":[makeQuery(id+"F1.opExtrude","CAP_FACE",FACE,{"disambiguationData":[OSD([sQuery(id+"F0.wireOp",EDGE,"E0"),sQuery(id+"F0.wireOp",EDGE,"E1"),sQuery(id+"F0.wireOp",EDGE,"E4"),sQuery(id+"F0.wireOp",EDGE,"E5"),sQuery(id+"F0.wireOp",EDGE,"E6"),sQuery(id+"F0.wireOp",EDGE,"E7"),sQuery(id+"F0.wireOp",EDGE,"E8"),sQuery(id+"F0.wireOp",EDGE,"E9"),subQ0,sQuery(id+"F0.wireOp",EDGE,"E11.MirrorCS"),sQuery(id+"F0.wireOp",EDGE,"E12.MirrorCS"),sQuery(id+"F0.wireOp",EDGE,"E13.MirrorCS"),sQuery(id+"F0.wireOp",EDGE,"E14.MirrorCS"),sQuery(id+"F0.wireOp",EDGE,"E15.MirrorCS"),sQuery(id+"F0.wireOp",EDGE,"E16.MirrorCS"),sQuery(id+"F0.wireOp",EDGE,"E17.MirrorCS"),sQuery(id+"F0.wireOp",EDGE,"E18.MirrorCS"),sQuery(id+"F0.wireOp",EDGE,"E19"),sQuery(id+"F0.wireOp",EDGE,"E20.MirrorCS"),sQuery(id+"F0.wireOp",EDGE,"E21"),sQuery(id+"F0.wireOp",EDGE,"E22.MirrorCS")])],"isStart":true})]});}
            chamfer(context, id + "F8", {"entities" : qUnion([Q0, Q1, Q2, Q3, Q4, Q5, Q6, Q7, Q8, Q9]), "width" : 5 * mm, "tangentPropagation" : true});
        }
        {
            var Q0;
            {var subQ0=sQuery(id+"F0.wireOp",EDGE,"E0");Q0=makeQuery(id+"F2.opChamfer","BLEND_EDGE",EDGE,{"blendedFrom":[makeQuery(id+"F1.opExtrude","CAP_EDGE",EDGE,{"disambiguationData":[OSD([subQ0])],"isStart":false}),makeQuery(id+"F1.opExtrude","CAP_FACE",FACE,{"disambiguationData":[OSD([subQ0,sQuery(id+"F0.wireOp",EDGE,"E1"),sQuery(id+"F0.wireOp",EDGE,"E4"),sQuery(id+"F0.wireOp",EDGE,"E5"),sQuery(id+"F0.wireOp",EDGE,"E6"),sQuery(id+"F0.wireOp",EDGE,"E7"),sQuery(id+"F0.wireOp",EDGE,"E8"),sQuery(id+"F0.wireOp",EDGE,"E9"),sQuery(id+"F0.wireOp",EDGE,"E10"),sQuery(id+"F0.wireOp",EDGE,"E11.MirrorCS"),sQuery(id+"F0.wireOp",EDGE,"E12.MirrorCS"),sQuery(id+"F0.wireOp",EDGE,"E13.MirrorCS"),sQuery(id+"F0.wireOp",EDGE,"E14.MirrorCS"),sQuery(id+"F0.wireOp",EDGE,"E15.MirrorCS"),sQuery(id+"F0.wireOp",EDGE,"E16.MirrorCS"),sQuery(id+"F0.wireOp",EDGE,"E17.MirrorCS"),sQuery(id+"F0.wireOp",EDGE,"E18.MirrorCS"),sQuery(id+"F0.wireOp",EDGE,"E19"),sQuery(id+"F0.wireOp",EDGE,"E20.MirrorCS"),sQuery(id+"F0.wireOp",EDGE,"E21"),sQuery(id+"F0.wireOp",EDGE,"E22.MirrorCS")])],"isStart":false})],"blendedInto":[makeQuery(id+"F1.opExtrude","CAP_FACE",FACE,{"disambiguationData":[OSD([subQ0,sQuery(id+"F0.wireOp",EDGE,"E1"),sQuery(id+"F0.wireOp",EDGE,"E4"),sQuery(id+"F0.wireOp",EDGE,"E5"),sQuery(id+"F0.wireOp",EDGE,"E6"),sQuery(id+"F0.wireOp",EDGE,"E7"),sQuery(id+"F0.wireOp",EDGE,"E8"),sQuery(id+"F0.wireOp",EDGE,"E9"),sQuery(id+"F0.wireOp",EDGE,"E10"),sQuery(id+"F0.wireOp",EDGE,"E11.MirrorCS"),sQuery(id+"F0.wireOp",EDGE,"E12.MirrorCS"),sQuery(id+"F0.wireOp",EDGE,"E13.MirrorCS"),sQuery(id+"F0.wireOp",EDGE,"E14.MirrorCS"),sQuery(id+"F0.wireOp",EDGE,"E15.MirrorCS"),sQuery(id+"F0.wireOp",EDGE,"E16.MirrorCS"),sQuery(id+"F0.wireOp",EDGE,"E17.MirrorCS"),sQuery(id+"F0.wireOp",EDGE,"E18.MirrorCS"),sQuery(id+"F0.wireOp",EDGE,"E19"),sQuery(id+"F0.wireOp",EDGE,"E20.MirrorCS"),sQuery(id+"F0.wireOp",EDGE,"E21"),sQuery(id+"F0.wireOp",EDGE,"E22.MirrorCS")])],"isStart":false})]});}
            var Q1;
            {var subQ0=sQuery(id+"F0.wireOp",EDGE,"E7");Q1=makeQuery(id+"F2.opChamfer","BLEND_EDGE",EDGE,{"blendedFrom":[makeQuery(id+"F1.opExtrude","CAP_EDGE",EDGE,{"disambiguationData":[OSD([subQ0])],"isStart":false}),makeQuery(id+"F1.opExtrude","CAP_FACE",FACE,{"disambiguationData":[OSD([sQuery(id+"F0.wireOp",EDGE,"E0"),sQuery(id+"F0.wireOp",EDGE,"E1"),sQuery(id+"F0.wireOp",EDGE,"E4"),sQuery(id+"F0.wireOp",EDGE,"E5"),sQuery(id+"F0.wireOp",EDGE,"E6"),subQ0,sQuery(id+"F0.wireOp",EDGE,"E8"),sQuery(id+"F0.wireOp",EDGE,"E9"),sQuery(id+"F0.wireOp",EDGE,"E10"),sQuery(id+"F0.wireOp",EDGE,"E11.MirrorCS"),sQuery(id+"F0.wireOp",EDGE,"E12.MirrorCS"),sQuery(id+"F0.wireOp",EDGE,"E13.MirrorCS"),sQuery(id+"F0.wireOp",EDGE,"E14.MirrorCS"),sQuery(id+"F0.wireOp",EDGE,"E15.MirrorCS"),sQuery(id+"F0.wireOp",EDGE,"E16.MirrorCS"),sQuery(id+"F0.wireOp",EDGE,"E17.MirrorCS"),sQuery(id+"F0.wireOp",EDGE,"E18.MirrorCS"),sQuery(id+"F0.wireOp",EDGE,"E19"),sQuery(id+"F0.wireOp",EDGE,"E20.MirrorCS"),sQuery(id+"F0.wireOp",EDGE,"E21"),sQuery(id+"F0.wireOp",EDGE,"E22.MirrorCS")])],"isStart":false})],"blendedInto":[makeQuery(id+"F1.opExtrude","CAP_FACE",FACE,{"disambiguationData":[OSD([sQuery(id+"F0.wireOp",EDGE,"E0"),sQuery(id+"F0.wireOp",EDGE,"E1"),sQuery(id+"F0.wireOp",EDGE,"E4"),sQuery(id+"F0.wireOp",EDGE,"E5"),sQuery(id+"F0.wireOp",EDGE,"E6"),subQ0,sQuery(id+"F0.wireOp",EDGE,"E8"),sQuery(id+"F0.wireOp",EDGE,"E9"),sQuery(id+"F0.wireOp",EDGE,"E10"),sQuery(id+"F0.wireOp",EDGE,"E11.MirrorCS"),sQuery(id+"F0.wireOp",EDGE,"E12.MirrorCS"),sQuery(id+"F0.wireOp",EDGE,"E13.MirrorCS"),sQuery(id+"F0.wireOp",EDGE,"E14.MirrorCS"),sQuery(id+"F0.wireOp",EDGE,"E15.MirrorCS"),sQuery(id+"F0.wireOp",EDGE,"E16.MirrorCS"),sQuery(id+"F0.wireOp",EDGE,"E17.MirrorCS"),sQuery(id+"F0.wireOp",EDGE,"E18.MirrorCS"),sQuery(id+"F0.wireOp",EDGE,"E19"),sQuery(id+"F0.wireOp",EDGE,"E20.MirrorCS"),sQuery(id+"F0.wireOp",EDGE,"E21"),sQuery(id+"F0.wireOp",EDGE,"E22.MirrorCS")])],"isStart":false})]});}
            var Q2;
            {var subQ0=sQuery(id+"F0.wireOp",EDGE,"E10");Q2=makeQuery(id+"F2.opChamfer","BLEND_EDGE",EDGE,{"blendedFrom":[makeQuery(id+"F1.opExtrude","CAP_EDGE",EDGE,{"disambiguationData":[OSD([subQ0])],"isStart":false}),makeQuery(id+"F1.opExtrude","CAP_FACE",FACE,{"disambiguationData":[OSD([sQuery(id+"F0.wireOp",EDGE,"E0"),sQuery(id+"F0.wireOp",EDGE,"E1"),sQuery(id+"F0.wireOp",EDGE,"E4"),sQuery(id+"F0.wireOp",EDGE,"E5"),sQuery(id+"F0.wireOp",EDGE,"E6"),sQuery(id+"F0.wireOp",EDGE,"E7"),sQuery(id+"F0.wireOp",EDGE,"E8"),sQuery(id+"F0.wireOp",EDGE,"E9"),subQ0,sQuery(id+"F0.wireOp",EDGE,"E11.MirrorCS"),sQuery(id+"F0.wireOp",EDGE,"E12.MirrorCS"),sQuery(id+"F0.wireOp",EDGE,"E13.MirrorCS"),sQuery(id+"F0.wireOp",EDGE,"E14.MirrorCS"),sQuery(id+"F0.wireOp",EDGE,"E15.MirrorCS"),sQuery(id+"F0.wireOp",EDGE,"E16.MirrorCS"),sQuery(id+"F0.wireOp",EDGE,"E17.MirrorCS"),sQuery(id+"F0.wireOp",EDGE,"E18.MirrorCS"),sQuery(id+"F0.wireOp",EDGE,"E19"),sQuery(id+"F0.wireOp",EDGE,"E20.MirrorCS"),sQuery(id+"F0.wireOp",EDGE,"E21"),sQuery(id+"F0.wireOp",EDGE,"E22.MirrorCS")])],"isStart":false})],"blendedInto":[makeQuery(id+"F1.opExtrude","CAP_FACE",FACE,{"disambiguationData":[OSD([sQuery(id+"F0.wireOp",EDGE,"E0"),sQuery(id+"F0.wireOp",EDGE,"E1"),sQuery(id+"F0.wireOp",EDGE,"E4"),sQuery(id+"F0.wireOp",EDGE,"E5"),sQuery(id+"F0.wireOp",EDGE,"E6"),sQuery(id+"F0.wireOp",EDGE,"E7"),sQuery(id+"F0.wireOp",EDGE,"E8"),sQuery(id+"F0.wireOp",EDGE,"E9"),subQ0,sQuery(id+"F0.wireOp",EDGE,"E11.MirrorCS"),sQuery(id+"F0.wireOp",EDGE,"E12.MirrorCS"),sQuery(id+"F0.wireOp",EDGE,"E13.MirrorCS"),sQuery(id+"F0.wireOp",EDGE,"E14.MirrorCS"),sQuery(id+"F0.wireOp",EDGE,"E15.MirrorCS"),sQuery(id+"F0.wireOp",EDGE,"E16.MirrorCS"),sQuery(id+"F0.wireOp",EDGE,"E17.MirrorCS"),sQuery(id+"F0.wireOp",EDGE,"E18.MirrorCS"),sQuery(id+"F0.wireOp",EDGE,"E19"),sQuery(id+"F0.wireOp",EDGE,"E20.MirrorCS"),sQuery(id+"F0.wireOp",EDGE,"E21"),sQuery(id+"F0.wireOp",EDGE,"E22.MirrorCS")])],"isStart":false})]});}
            var Q3;
            {var subQ0=sQuery(id+"F0.wireOp",EDGE,"E1");Q3=makeQuery(id+"F4.opChamfer","BLEND_EDGE",EDGE,{"blendedFrom":[makeQuery(id+"F1.opExtrude","CAP_EDGE",EDGE,{"disambiguationData":[OSD([subQ0])],"isStart":false}),makeQuery(id+"F1.opExtrude","CAP_FACE",FACE,{"disambiguationData":[OSD([sQuery(id+"F0.wireOp",EDGE,"E0"),subQ0,sQuery(id+"F0.wireOp",EDGE,"E4"),sQuery(id+"F0.wireOp",EDGE,"E5"),sQuery(id+"F0.wireOp",EDGE,"E6"),sQuery(id+"F0.wireOp",EDGE,"E7"),sQuery(id+"F0.wireOp",EDGE,"E8"),sQuery(id+"F0.wireOp",EDGE,"E9"),sQuery(id+"F0.wireOp",EDGE,"E10"),sQuery(id+"F0.wireOp",EDGE,"E11.MirrorCS"),sQuery(id+"F0.wireOp",EDGE,"E12.MirrorCS"),sQuery(id+"F0.wireOp",EDGE,"E13.MirrorCS"),sQuery(id+"F0.wireOp",EDGE,"E14.MirrorCS"),sQuery(id+"F0.wireOp",EDGE,"E15.MirrorCS"),sQuery(id+"F0.wireOp",EDGE,"E16.MirrorCS"),sQuery(id+"F0.wireOp",EDGE,"E17.MirrorCS"),sQuery(id+"F0.wireOp",EDGE,"E18.MirrorCS"),sQuery(id+"F0.wireOp",EDGE,"E19"),sQuery(id+"F0.wireOp",EDGE,"E20.MirrorCS"),sQuery(id+"F0.wireOp",EDGE,"E21"),sQuery(id+"F0.wireOp",EDGE,"E22.MirrorCS")])],"isStart":false})],"blendedInto":[makeQuery(id+"F1.opExtrude","CAP_FACE",FACE,{"disambiguationData":[OSD([sQuery(id+"F0.wireOp",EDGE,"E0"),subQ0,sQuery(id+"F0.wireOp",EDGE,"E4"),sQuery(id+"F0.wireOp",EDGE,"E5"),sQuery(id+"F0.wireOp",EDGE,"E6"),sQuery(id+"F0.wireOp",EDGE,"E7"),sQuery(id+"F0.wireOp",EDGE,"E8"),sQuery(id+"F0.wireOp",EDGE,"E9"),sQuery(id+"F0.wireOp",EDGE,"E10"),sQuery(id+"F0.wireOp",EDGE,"E11.MirrorCS"),sQuery(id+"F0.wireOp",EDGE,"E12.MirrorCS"),sQuery(id+"F0.wireOp",EDGE,"E13.MirrorCS"),sQuery(id+"F0.wireOp",EDGE,"E14.MirrorCS"),sQuery(id+"F0.wireOp",EDGE,"E15.MirrorCS"),sQuery(id+"F0.wireOp",EDGE,"E16.MirrorCS"),sQuery(id+"F0.wireOp",EDGE,"E17.MirrorCS"),sQuery(id+"F0.wireOp",EDGE,"E18.MirrorCS"),sQuery(id+"F0.wireOp",EDGE,"E19"),sQuery(id+"F0.wireOp",EDGE,"E20.MirrorCS"),sQuery(id+"F0.wireOp",EDGE,"E21"),sQuery(id+"F0.wireOp",EDGE,"E22.MirrorCS")])],"isStart":false})]});}
            var Q4;
            {var subQ0=sQuery(id+"F0.wireOp",EDGE,"E19");Q4=makeQuery(id+"F3.opChamfer","BLEND_EDGE",EDGE,{"blendedFrom":[makeQuery(id+"F1.opExtrude","CAP_EDGE",EDGE,{"disambiguationData":[OSD([subQ0])],"isStart":false}),makeQuery(id+"F1.opExtrude","CAP_FACE",FACE,{"disambiguationData":[OSD([sQuery(id+"F0.wireOp",EDGE,"E0"),sQuery(id+"F0.wireOp",EDGE,"E1"),sQuery(id+"F0.wireOp",EDGE,"E4"),sQuery(id+"F0.wireOp",EDGE,"E5"),sQuery(id+"F0.wireOp",EDGE,"E6"),sQuery(id+"F0.wireOp",EDGE,"E7"),sQuery(id+"F0.wireOp",EDGE,"E8"),sQuery(id+"F0.wireOp",EDGE,"E9"),sQuery(id+"F0.wireOp",EDGE,"E10"),sQuery(id+"F0.wireOp",EDGE,"E11.MirrorCS"),sQuery(id+"F0.wireOp",EDGE,"E12.MirrorCS"),sQuery(id+"F0.wireOp",EDGE,"E13.MirrorCS"),sQuery(id+"F0.wireOp",EDGE,"E14.MirrorCS"),sQuery(id+"F0.wireOp",EDGE,"E15.MirrorCS"),sQuery(id+"F0.wireOp",EDGE,"E16.MirrorCS"),sQuery(id+"F0.wireOp",EDGE,"E17.MirrorCS"),sQuery(id+"F0.wireOp",EDGE,"E18.MirrorCS"),subQ0,sQuery(id+"F0.wireOp",EDGE,"E20.MirrorCS"),sQuery(id+"F0.wireOp",EDGE,"E21"),sQuery(id+"F0.wireOp",EDGE,"E22.MirrorCS")])],"isStart":false})],"blendedInto":[makeQuery(id+"F1.opExtrude","CAP_FACE",FACE,{"disambiguationData":[OSD([sQuery(id+"F0.wireOp",EDGE,"E0"),sQuery(id+"F0.wireOp",EDGE,"E1"),sQuery(id+"F0.wireOp",EDGE,"E4"),sQuery(id+"F0.wireOp",EDGE,"E5"),sQuery(id+"F0.wireOp",EDGE,"E6"),sQuery(id+"F0.wireOp",EDGE,"E7"),sQuery(id+"F0.wireOp",EDGE,"E8"),sQuery(id+"F0.wireOp",EDGE,"E9"),sQuery(id+"F0.wireOp",EDGE,"E10"),sQuery(id+"F0.wireOp",EDGE,"E11.MirrorCS"),sQuery(id+"F0.wireOp",EDGE,"E12.MirrorCS"),sQuery(id+"F0.wireOp",EDGE,"E13.MirrorCS"),sQuery(id+"F0.wireOp",EDGE,"E14.MirrorCS"),sQuery(id+"F0.wireOp",EDGE,"E15.MirrorCS"),sQuery(id+"F0.wireOp",EDGE,"E16.MirrorCS"),sQuery(id+"F0.wireOp",EDGE,"E17.MirrorCS"),sQuery(id+"F0.wireOp",EDGE,"E18.MirrorCS"),subQ0,sQuery(id+"F0.wireOp",EDGE,"E20.MirrorCS"),sQuery(id+"F0.wireOp",EDGE,"E21"),sQuery(id+"F0.wireOp",EDGE,"E22.MirrorCS")])],"isStart":false})]});}
            var Q5;
            {var subQ0=sQuery(id+"F0.wireOp",EDGE,"E21");Q5=makeQuery(id+"F6.opChamfer","BLEND_EDGE",EDGE,{"blendedFrom":[makeQuery(id+"F1.opExtrude","CAP_EDGE",EDGE,{"disambiguationData":[OSD([subQ0])],"isStart":false}),makeQuery(id+"F1.opExtrude","CAP_FACE",FACE,{"disambiguationData":[OSD([sQuery(id+"F0.wireOp",EDGE,"E0"),sQuery(id+"F0.wireOp",EDGE,"E1"),sQuery(id+"F0.wireOp",EDGE,"E4"),sQuery(id+"F0.wireOp",EDGE,"E5"),sQuery(id+"F0.wireOp",EDGE,"E6"),sQuery(id+"F0.wireOp",EDGE,"E7"),sQuery(id+"F0.wireOp",EDGE,"E8"),sQuery(id+"F0.wireOp",EDGE,"E9"),sQuery(id+"F0.wireOp",EDGE,"E10"),sQuery(id+"F0.wireOp",EDGE,"E11.MirrorCS"),sQuery(id+"F0.wireOp",EDGE,"E12.MirrorCS"),sQuery(id+"F0.wireOp",EDGE,"E13.MirrorCS"),sQuery(id+"F0.wireOp",EDGE,"E14.MirrorCS"),sQuery(id+"F0.wireOp",EDGE,"E15.MirrorCS"),sQuery(id+"F0.wireOp",EDGE,"E16.MirrorCS"),sQuery(id+"F0.wireOp",EDGE,"E17.MirrorCS"),sQuery(id+"F0.wireOp",EDGE,"E18.MirrorCS"),sQuery(id+"F0.wireOp",EDGE,"E19"),sQuery(id+"F0.wireOp",EDGE,"E20.MirrorCS"),subQ0,sQuery(id+"F0.wireOp",EDGE,"E22.MirrorCS")])],"isStart":false})],"blendedInto":[makeQuery(id+"F1.opExtrude","CAP_FACE",FACE,{"disambiguationData":[OSD([sQuery(id+"F0.wireOp",EDGE,"E0"),sQuery(id+"F0.wireOp",EDGE,"E1"),sQuery(id+"F0.wireOp",EDGE,"E4"),sQuery(id+"F0.wireOp",EDGE,"E5"),sQuery(id+"F0.wireOp",EDGE,"E6"),sQuery(id+"F0.wireOp",EDGE,"E7"),sQuery(id+"F0.wireOp",EDGE,"E8"),sQuery(id+"F0.wireOp",EDGE,"E9"),sQuery(id+"F0.wireOp",EDGE,"E10"),sQuery(id+"F0.wireOp",EDGE,"E11.MirrorCS"),sQuery(id+"F0.wireOp",EDGE,"E12.MirrorCS"),sQuery(id+"F0.wireOp",EDGE,"E13.MirrorCS"),sQuery(id+"F0.wireOp",EDGE,"E14.MirrorCS"),sQuery(id+"F0.wireOp",EDGE,"E15.MirrorCS"),sQuery(id+"F0.wireOp",EDGE,"E16.MirrorCS"),sQuery(id+"F0.wireOp",EDGE,"E17.MirrorCS"),sQuery(id+"F0.wireOp",EDGE,"E18.MirrorCS"),sQuery(id+"F0.wireOp",EDGE,"E19"),sQuery(id+"F0.wireOp",EDGE,"E20.MirrorCS"),subQ0,sQuery(id+"F0.wireOp",EDGE,"E22.MirrorCS")])],"isStart":false})]});}
            var Q6;
            {var subQ0=sQuery(id+"F0.wireOp",EDGE,"E14.MirrorCS");Q6=makeQuery(id+"F6.opChamfer","BLEND_EDGE",EDGE,{"blendedFrom":[makeQuery(id+"F1.opExtrude","CAP_EDGE",EDGE,{"disambiguationData":[OSD([subQ0])],"isStart":false}),makeQuery(id+"F1.opExtrude","CAP_FACE",FACE,{"disambiguationData":[OSD([sQuery(id+"F0.wireOp",EDGE,"E0"),sQuery(id+"F0.wireOp",EDGE,"E1"),sQuery(id+"F0.wireOp",EDGE,"E4"),sQuery(id+"F0.wireOp",EDGE,"E5"),sQuery(id+"F0.wireOp",EDGE,"E6"),sQuery(id+"F0.wireOp",EDGE,"E7"),sQuery(id+"F0.wireOp",EDGE,"E8"),sQuery(id+"F0.wireOp",EDGE,"E9"),sQuery(id+"F0.wireOp",EDGE,"E10"),sQuery(id+"F0.wireOp",EDGE,"E11.MirrorCS"),sQuery(id+"F0.wireOp",EDGE,"E12.MirrorCS"),sQuery(id+"F0.wireOp",EDGE,"E13.MirrorCS"),subQ0,sQuery(id+"F0.wireOp",EDGE,"E15.MirrorCS"),sQuery(id+"F0.wireOp",EDGE,"E16.MirrorCS"),sQuery(id+"F0.wireOp",EDGE,"E17.MirrorCS"),sQuery(id+"F0.wireOp",EDGE,"E18.MirrorCS"),sQuery(id+"F0.wireOp",EDGE,"E19"),sQuery(id+"F0.wireOp",EDGE,"E20.MirrorCS"),sQuery(id+"F0.wireOp",EDGE,"E21"),sQuery(id+"F0.wireOp",EDGE,"E22.MirrorCS")])],"isStart":false})],"blendedInto":[makeQuery(id+"F1.opExtrude","CAP_FACE",FACE,{"disambiguationData":[OSD([sQuery(id+"F0.wireOp",EDGE,"E0"),sQuery(id+"F0.wireOp",EDGE,"E1"),sQuery(id+"F0.wireOp",EDGE,"E4"),sQuery(id+"F0.wireOp",EDGE,"E5"),sQuery(id+"F0.wireOp",EDGE,"E6"),sQuery(id+"F0.wireOp",EDGE,"E7"),sQuery(id+"F0.wireOp",EDGE,"E8"),sQuery(id+"F0.wireOp",EDGE,"E9"),sQuery(id+"F0.wireOp",EDGE,"E10"),sQuery(id+"F0.wireOp",EDGE,"E11.MirrorCS"),sQuery(id+"F0.wireOp",EDGE,"E12.MirrorCS"),sQuery(id+"F0.wireOp",EDGE,"E13.MirrorCS"),subQ0,sQuery(id+"F0.wireOp",EDGE,"E15.MirrorCS"),sQuery(id+"F0.wireOp",EDGE,"E16.MirrorCS"),sQuery(id+"F0.wireOp",EDGE,"E17.MirrorCS"),sQuery(id+"F0.wireOp",EDGE,"E18.MirrorCS"),sQuery(id+"F0.wireOp",EDGE,"E19"),sQuery(id+"F0.wireOp",EDGE,"E20.MirrorCS"),sQuery(id+"F0.wireOp",EDGE,"E21"),sQuery(id+"F0.wireOp",EDGE,"E22.MirrorCS")])],"isStart":false})]});}
            var Q7;
            {var subQ0=sQuery(id+"F0.wireOp",EDGE,"E22.MirrorCS");Q7=makeQuery(id+"F6.opChamfer","BLEND_EDGE",EDGE,{"blendedFrom":[makeQuery(id+"F1.opExtrude","CAP_EDGE",EDGE,{"disambiguationData":[OSD([subQ0])],"isStart":false}),makeQuery(id+"F1.opExtrude","CAP_FACE",FACE,{"disambiguationData":[OSD([sQuery(id+"F0.wireOp",EDGE,"E0"),sQuery(id+"F0.wireOp",EDGE,"E1"),sQuery(id+"F0.wireOp",EDGE,"E4"),sQuery(id+"F0.wireOp",EDGE,"E5"),sQuery(id+"F0.wireOp",EDGE,"E6"),sQuery(id+"F0.wireOp",EDGE,"E7"),sQuery(id+"F0.wireOp",EDGE,"E8"),sQuery(id+"F0.wireOp",EDGE,"E9"),sQuery(id+"F0.wireOp",EDGE,"E10"),sQuery(id+"F0.wireOp",EDGE,"E11.MirrorCS"),sQuery(id+"F0.wireOp",EDGE,"E12.MirrorCS"),sQuery(id+"F0.wireOp",EDGE,"E13.MirrorCS"),sQuery(id+"F0.wireOp",EDGE,"E14.MirrorCS"),sQuery(id+"F0.wireOp",EDGE,"E15.MirrorCS"),sQuery(id+"F0.wireOp",EDGE,"E16.MirrorCS"),sQuery(id+"F0.wireOp",EDGE,"E17.MirrorCS"),sQuery(id+"F0.wireOp",EDGE,"E18.MirrorCS"),sQuery(id+"F0.wireOp",EDGE,"E19"),sQuery(id+"F0.wireOp",EDGE,"E20.MirrorCS"),sQuery(id+"F0.wireOp",EDGE,"E21"),subQ0])],"isStart":false})],"blendedInto":[makeQuery(id+"F1.opExtrude","CAP_FACE",FACE,{"disambiguationData":[OSD([sQuery(id+"F0.wireOp",EDGE,"E0"),sQuery(id+"F0.wireOp",EDGE,"E1"),sQuery(id+"F0.wireOp",EDGE,"E4"),sQuery(id+"F0.wireOp",EDGE,"E5"),sQuery(id+"F0.wireOp",EDGE,"E6"),sQuery(id+"F0.wireOp",EDGE,"E7"),sQuery(id+"F0.wireOp",EDGE,"E8"),sQuery(id+"F0.wireOp",EDGE,"E9"),sQuery(id+"F0.wireOp",EDGE,"E10"),sQuery(id+"F0.wireOp",EDGE,"E11.MirrorCS"),sQuery(id+"F0.wireOp",EDGE,"E12.MirrorCS"),sQuery(id+"F0.wireOp",EDGE,"E13.MirrorCS"),sQuery(id+"F0.wireOp",EDGE,"E14.MirrorCS"),sQuery(id+"F0.wireOp",EDGE,"E15.MirrorCS"),sQuery(id+"F0.wireOp",EDGE,"E16.MirrorCS"),sQuery(id+"F0.wireOp",EDGE,"E17.MirrorCS"),sQuery(id+"F0.wireOp",EDGE,"E18.MirrorCS"),sQuery(id+"F0.wireOp",EDGE,"E19"),sQuery(id+"F0.wireOp",EDGE,"E20.MirrorCS"),sQuery(id+"F0.wireOp",EDGE,"E21"),subQ0])],"isStart":false})]});}
            var Q8;
            {var subQ0=sQuery(id+"F0.wireOp",EDGE,"E20.MirrorCS");Q8=makeQuery(id+"F6.opChamfer","BLEND_EDGE",EDGE,{"blendedFrom":[makeQuery(id+"F1.opExtrude","CAP_EDGE",EDGE,{"disambiguationData":[OSD([subQ0])],"isStart":false}),makeQuery(id+"F1.opExtrude","CAP_FACE",FACE,{"disambiguationData":[OSD([sQuery(id+"F0.wireOp",EDGE,"E0"),sQuery(id+"F0.wireOp",EDGE,"E1"),sQuery(id+"F0.wireOp",EDGE,"E4"),sQuery(id+"F0.wireOp",EDGE,"E5"),sQuery(id+"F0.wireOp",EDGE,"E6"),sQuery(id+"F0.wireOp",EDGE,"E7"),sQuery(id+"F0.wireOp",EDGE,"E8"),sQuery(id+"F0.wireOp",EDGE,"E9"),sQuery(id+"F0.wireOp",EDGE,"E10"),sQuery(id+"F0.wireOp",EDGE,"E11.MirrorCS"),sQuery(id+"F0.wireOp",EDGE,"E12.MirrorCS"),sQuery(id+"F0.wireOp",EDGE,"E13.MirrorCS"),sQuery(id+"F0.wireOp",EDGE,"E14.MirrorCS"),sQuery(id+"F0.wireOp",EDGE,"E15.MirrorCS"),sQuery(id+"F0.wireOp",EDGE,"E16.MirrorCS"),sQuery(id+"F0.wireOp",EDGE,"E17.MirrorCS"),sQuery(id+"F0.wireOp",EDGE,"E18.MirrorCS"),sQuery(id+"F0.wireOp",EDGE,"E19"),subQ0,sQuery(id+"F0.wireOp",EDGE,"E21"),sQuery(id+"F0.wireOp",EDGE,"E22.MirrorCS")])],"isStart":false})],"blendedInto":[makeQuery(id+"F1.opExtrude","CAP_FACE",FACE,{"disambiguationData":[OSD([sQuery(id+"F0.wireOp",EDGE,"E0"),sQuery(id+"F0.wireOp",EDGE,"E1"),sQuery(id+"F0.wireOp",EDGE,"E4"),sQuery(id+"F0.wireOp",EDGE,"E5"),sQuery(id+"F0.wireOp",EDGE,"E6"),sQuery(id+"F0.wireOp",EDGE,"E7"),sQuery(id+"F0.wireOp",EDGE,"E8"),sQuery(id+"F0.wireOp",EDGE,"E9"),sQuery(id+"F0.wireOp",EDGE,"E10"),sQuery(id+"F0.wireOp",EDGE,"E11.MirrorCS"),sQuery(id+"F0.wireOp",EDGE,"E12.MirrorCS"),sQuery(id+"F0.wireOp",EDGE,"E13.MirrorCS"),sQuery(id+"F0.wireOp",EDGE,"E14.MirrorCS"),sQuery(id+"F0.wireOp",EDGE,"E15.MirrorCS"),sQuery(id+"F0.wireOp",EDGE,"E16.MirrorCS"),sQuery(id+"F0.wireOp",EDGE,"E17.MirrorCS"),sQuery(id+"F0.wireOp",EDGE,"E18.MirrorCS"),sQuery(id+"F0.wireOp",EDGE,"E19"),subQ0,sQuery(id+"F0.wireOp",EDGE,"E21"),sQuery(id+"F0.wireOp",EDGE,"E22.MirrorCS")])],"isStart":false})]});}
            var Q9;
            {var subQ0=sQuery(id+"F0.wireOp",EDGE,"E13.MirrorCS");Q9=makeQuery(id+"F5.opChamfer","BLEND_EDGE",EDGE,{"blendedFrom":[makeQuery(id+"F1.opExtrude","CAP_EDGE",EDGE,{"disambiguationData":[OSD([subQ0])],"isStart":false}),makeQuery(id+"F1.opExtrude","CAP_FACE",FACE,{"disambiguationData":[OSD([sQuery(id+"F0.wireOp",EDGE,"E0"),sQuery(id+"F0.wireOp",EDGE,"E1"),sQuery(id+"F0.wireOp",EDGE,"E4"),sQuery(id+"F0.wireOp",EDGE,"E5"),sQuery(id+"F0.wireOp",EDGE,"E6"),sQuery(id+"F0.wireOp",EDGE,"E7"),sQuery(id+"F0.wireOp",EDGE,"E8"),sQuery(id+"F0.wireOp",EDGE,"E9"),sQuery(id+"F0.wireOp",EDGE,"E10"),sQuery(id+"F0.wireOp",EDGE,"E11.MirrorCS"),sQuery(id+"F0.wireOp",EDGE,"E12.MirrorCS"),subQ0,sQuery(id+"F0.wireOp",EDGE,"E14.MirrorCS"),sQuery(id+"F0.wireOp",EDGE,"E15.MirrorCS"),sQuery(id+"F0.wireOp",EDGE,"E16.MirrorCS"),sQuery(id+"F0.wireOp",EDGE,"E17.MirrorCS"),sQuery(id+"F0.wireOp",EDGE,"E18.MirrorCS"),sQuery(id+"F0.wireOp",EDGE,"E19"),sQuery(id+"F0.wireOp",EDGE,"E20.MirrorCS"),sQuery(id+"F0.wireOp",EDGE,"E21"),sQuery(id+"F0.wireOp",EDGE,"E22.MirrorCS")])],"isStart":false})],"blendedInto":[makeQuery(id+"F1.opExtrude","CAP_FACE",FACE,{"disambiguationData":[OSD([sQuery(id+"F0.wireOp",EDGE,"E0"),sQuery(id+"F0.wireOp",EDGE,"E1"),sQuery(id+"F0.wireOp",EDGE,"E4"),sQuery(id+"F0.wireOp",EDGE,"E5"),sQuery(id+"F0.wireOp",EDGE,"E6"),sQuery(id+"F0.wireOp",EDGE,"E7"),sQuery(id+"F0.wireOp",EDGE,"E8"),sQuery(id+"F0.wireOp",EDGE,"E9"),sQuery(id+"F0.wireOp",EDGE,"E10"),sQuery(id+"F0.wireOp",EDGE,"E11.MirrorCS"),sQuery(id+"F0.wireOp",EDGE,"E12.MirrorCS"),subQ0,sQuery(id+"F0.wireOp",EDGE,"E14.MirrorCS"),sQuery(id+"F0.wireOp",EDGE,"E15.MirrorCS"),sQuery(id+"F0.wireOp",EDGE,"E16.MirrorCS"),sQuery(id+"F0.wireOp",EDGE,"E17.MirrorCS"),sQuery(id+"F0.wireOp",EDGE,"E18.MirrorCS"),sQuery(id+"F0.wireOp",EDGE,"E19"),sQuery(id+"F0.wireOp",EDGE,"E20.MirrorCS"),sQuery(id+"F0.wireOp",EDGE,"E21"),sQuery(id+"F0.wireOp",EDGE,"E22.MirrorCS")])],"isStart":false})]});}
            var Q10;
            {var subQ0=sQuery(id+"F0.wireOp",EDGE,"E12.MirrorCS");Q10=makeQuery(id+"F5.opChamfer","BLEND_EDGE",EDGE,{"blendedFrom":[makeQuery(id+"F1.opExtrude","CAP_EDGE",EDGE,{"disambiguationData":[OSD([subQ0])],"isStart":false}),makeQuery(id+"F1.opExtrude","CAP_FACE",FACE,{"disambiguationData":[OSD([sQuery(id+"F0.wireOp",EDGE,"E0"),sQuery(id+"F0.wireOp",EDGE,"E1"),sQuery(id+"F0.wireOp",EDGE,"E4"),sQuery(id+"F0.wireOp",EDGE,"E5"),sQuery(id+"F0.wireOp",EDGE,"E6"),sQuery(id+"F0.wireOp",EDGE,"E7"),sQuery(id+"F0.wireOp",EDGE,"E8"),sQuery(id+"F0.wireOp",EDGE,"E9"),sQuery(id+"F0.wireOp",EDGE,"E10"),sQuery(id+"F0.wireOp",EDGE,"E11.MirrorCS"),subQ0,sQuery(id+"F0.wireOp",EDGE,"E13.MirrorCS"),sQuery(id+"F0.wireOp",EDGE,"E14.MirrorCS"),sQuery(id+"F0.wireOp",EDGE,"E15.MirrorCS"),sQuery(id+"F0.wireOp",EDGE,"E16.MirrorCS"),sQuery(id+"F0.wireOp",EDGE,"E17.MirrorCS"),sQuery(id+"F0.wireOp",EDGE,"E18.MirrorCS"),sQuery(id+"F0.wireOp",EDGE,"E19"),sQuery(id+"F0.wireOp",EDGE,"E20.MirrorCS"),sQuery(id+"F0.wireOp",EDGE,"E21"),sQuery(id+"F0.wireOp",EDGE,"E22.MirrorCS")])],"isStart":false})],"blendedInto":[makeQuery(id+"F1.opExtrude","CAP_FACE",FACE,{"disambiguationData":[OSD([sQuery(id+"F0.wireOp",EDGE,"E0"),sQuery(id+"F0.wireOp",EDGE,"E1"),sQuery(id+"F0.wireOp",EDGE,"E4"),sQuery(id+"F0.wireOp",EDGE,"E5"),sQuery(id+"F0.wireOp",EDGE,"E6"),sQuery(id+"F0.wireOp",EDGE,"E7"),sQuery(id+"F0.wireOp",EDGE,"E8"),sQuery(id+"F0.wireOp",EDGE,"E9"),sQuery(id+"F0.wireOp",EDGE,"E10"),sQuery(id+"F0.wireOp",EDGE,"E11.MirrorCS"),subQ0,sQuery(id+"F0.wireOp",EDGE,"E13.MirrorCS"),sQuery(id+"F0.wireOp",EDGE,"E14.MirrorCS"),sQuery(id+"F0.wireOp",EDGE,"E15.MirrorCS"),sQuery(id+"F0.wireOp",EDGE,"E16.MirrorCS"),sQuery(id+"F0.wireOp",EDGE,"E17.MirrorCS"),sQuery(id+"F0.wireOp",EDGE,"E18.MirrorCS"),sQuery(id+"F0.wireOp",EDGE,"E19"),sQuery(id+"F0.wireOp",EDGE,"E20.MirrorCS"),sQuery(id+"F0.wireOp",EDGE,"E21"),sQuery(id+"F0.wireOp",EDGE,"E22.MirrorCS")])],"isStart":false})]});}
            var Q11;
            {var subQ0=sQuery(id+"F0.wireOp",EDGE,"E17.MirrorCS");Q11=makeQuery(id+"F5.opChamfer","BLEND_EDGE",EDGE,{"blendedFrom":[makeQuery(id+"F1.opExtrude","CAP_EDGE",EDGE,{"disambiguationData":[OSD([subQ0])],"isStart":false}),makeQuery(id+"F1.opExtrude","CAP_FACE",FACE,{"disambiguationData":[OSD([sQuery(id+"F0.wireOp",EDGE,"E0"),sQuery(id+"F0.wireOp",EDGE,"E1"),sQuery(id+"F0.wireOp",EDGE,"E4"),sQuery(id+"F0.wireOp",EDGE,"E5"),sQuery(id+"F0.wireOp",EDGE,"E6"),sQuery(id+"F0.wireOp",EDGE,"E7"),sQuery(id+"F0.wireOp",EDGE,"E8"),sQuery(id+"F0.wireOp",EDGE,"E9"),sQuery(id+"F0.wireOp",EDGE,"E10"),sQuery(id+"F0.wireOp",EDGE,"E11.MirrorCS"),sQuery(id+"F0.wireOp",EDGE,"E12.MirrorCS"),sQuery(id+"F0.wireOp",EDGE,"E13.MirrorCS"),sQuery(id+"F0.wireOp",EDGE,"E14.MirrorCS"),sQuery(id+"F0.wireOp",EDGE,"E15.MirrorCS"),sQuery(id+"F0.wireOp",EDGE,"E16.MirrorCS"),subQ0,sQuery(id+"F0.wireOp",EDGE,"E18.MirrorCS"),sQuery(id+"F0.wireOp",EDGE,"E19"),sQuery(id+"F0.wireOp",EDGE,"E20.MirrorCS"),sQuery(id+"F0.wireOp",EDGE,"E21"),sQuery(id+"F0.wireOp",EDGE,"E22.MirrorCS")])],"isStart":false})],"blendedInto":[makeQuery(id+"F1.opExtrude","CAP_FACE",FACE,{"disambiguationData":[OSD([sQuery(id+"F0.wireOp",EDGE,"E0"),sQuery(id+"F0.wireOp",EDGE,"E1"),sQuery(id+"F0.wireOp",EDGE,"E4"),sQuery(id+"F0.wireOp",EDGE,"E5"),sQuery(id+"F0.wireOp",EDGE,"E6"),sQuery(id+"F0.wireOp",EDGE,"E7"),sQuery(id+"F0.wireOp",EDGE,"E8"),sQuery(id+"F0.wireOp",EDGE,"E9"),sQuery(id+"F0.wireOp",EDGE,"E10"),sQuery(id+"F0.wireOp",EDGE,"E11.MirrorCS"),sQuery(id+"F0.wireOp",EDGE,"E12.MirrorCS"),sQuery(id+"F0.wireOp",EDGE,"E13.MirrorCS"),sQuery(id+"F0.wireOp",EDGE,"E14.MirrorCS"),sQuery(id+"F0.wireOp",EDGE,"E15.MirrorCS"),sQuery(id+"F0.wireOp",EDGE,"E16.MirrorCS"),subQ0,sQuery(id+"F0.wireOp",EDGE,"E18.MirrorCS"),sQuery(id+"F0.wireOp",EDGE,"E19"),sQuery(id+"F0.wireOp",EDGE,"E20.MirrorCS"),sQuery(id+"F0.wireOp",EDGE,"E21"),sQuery(id+"F0.wireOp",EDGE,"E22.MirrorCS")])],"isStart":false})]});}
            chamfer(context, id + "F9", {"entities" : qUnion([Q0, Q1, Q2, Q3, Q4, Q5, Q6, Q7, Q8, Q9, Q10, Q11]), "width" : 5 * mm, "tangentPropagation" : true});
        }
        {
            var Q0;
            Q0=makeQuery(id+"F1.opExtrude","CAP_EDGE",EDGE,{"disambiguationData":[OSD([sQuery(id+"F0.wireOp",EDGE,"E12.MirrorCS")])],"isStart":false});
            var Q1;
            Q1=makeQuery(id+"F1.opExtrude","CAP_EDGE",EDGE,{"disambiguationData":[OSD([sQuery(id+"F0.wireOp",EDGE,"E12.MirrorCS")])],"isStart":true});
            var Q2;
            Q2=makeQuery(id+"F1.opExtrude","CAP_EDGE",EDGE,{"disambiguationData":[OSD([sQuery(id+"F0.wireOp",EDGE,"E11.MirrorCS")])],"isStart":false});
            var Q3;
            Q3=makeQuery(id+"F1.opExtrude","CAP_EDGE",EDGE,{"disambiguationData":[OSD([sQuery(id+"F0.wireOp",EDGE,"E15.MirrorCS")])],"isStart":false});
            var Q4;
            Q4=makeQuery(id+"F1.opExtrude","CAP_EDGE",EDGE,{"disambiguationData":[OSD([sQuery(id+"F0.wireOp",EDGE,"E15.MirrorCS")])],"isStart":true});
            chamfer(context, id + "F10", {"entities" : qUnion([Q0, Q1, Q2, Q3, Q4]), "width" : 2.5 * mm, "tangentPropagation" : true});
        }
        {
            var Q0;
            Q0=makeQuery(id+"F1.opExtrude","CAP_EDGE",EDGE,{"disambiguationData":[OSD([sQuery(id+"F0.wireOp",EDGE,"E7")])],"isStart":false});
            var Q1;
            Q1=makeQuery(id+"F1.opExtrude","CAP_EDGE",EDGE,{"disambiguationData":[OSD([sQuery(id+"F0.wireOp",EDGE,"E7")])],"isStart":true});
            var Q2;
            Q2=makeQuery(id+"F1.opExtrude","CAP_EDGE",EDGE,{"disambiguationData":[OSD([sQuery(id+"F0.wireOp",EDGE,"E8")])],"isStart":false});
            var Q3;
            Q3=makeQuery(id+"F1.opExtrude","CAP_EDGE",EDGE,{"disambiguationData":[OSD([sQuery(id+"F0.wireOp",EDGE,"E8")])],"isStart":true});
            chamfer(context, id + "F11", {"entities" : qUnion([Q0, Q1, Q2, Q3]), "width" : 2.5 * mm, "tangentPropagation" : true});
        }
        {
            var Q0;
            {var subQ0=sQuery(id+"F0.wireOp",EDGE,"E7");Q0=makeQuery(id+"F11.opChamfer","BLEND_EDGE",EDGE,{"blendedFrom":[makeQuery(id+"F1.opExtrude","CAP_EDGE",EDGE,{"disambiguationData":[OSD([subQ0])],"isStart":true}),makeQuery(id+"F1.opExtrude","CAP_FACE",FACE,{"disambiguationData":[OSD([sQuery(id+"F0.wireOp",EDGE,"E0"),sQuery(id+"F0.wireOp",EDGE,"E1"),sQuery(id+"F0.wireOp",EDGE,"E4"),sQuery(id+"F0.wireOp",EDGE,"E5"),sQuery(id+"F0.wireOp",EDGE,"E6"),subQ0,sQuery(id+"F0.wireOp",EDGE,"E8"),sQuery(id+"F0.wireOp",EDGE,"E9"),sQuery(id+"F0.wireOp",EDGE,"E10"),sQuery(id+"F0.wireOp",EDGE,"E11.MirrorCS"),sQuery(id+"F0.wireOp",EDGE,"E12.MirrorCS"),sQuery(id+"F0.wireOp",EDGE,"E13.MirrorCS"),sQuery(id+"F0.wireOp",EDGE,"E14.MirrorCS"),sQuery(id+"F0.wireOp",EDGE,"E15.MirrorCS"),sQuery(id+"F0.wireOp",EDGE,"E16.MirrorCS"),sQuery(id+"F0.wireOp",EDGE,"E17.MirrorCS"),sQuery(id+"F0.wireOp",EDGE,"E18.MirrorCS"),sQuery(id+"F0.wireOp",EDGE,"E19"),sQuery(id+"F0.wireOp",EDGE,"E20.MirrorCS"),sQuery(id+"F0.wireOp",EDGE,"E21"),sQuery(id+"F0.wireOp",EDGE,"E22.MirrorCS")])],"isStart":true})],"blendedInto":[makeQuery(id+"F1.opExtrude","CAP_FACE",FACE,{"disambiguationData":[OSD([sQuery(id+"F0.wireOp",EDGE,"E0"),sQuery(id+"F0.wireOp",EDGE,"E1"),sQuery(id+"F0.wireOp",EDGE,"E4"),sQuery(id+"F0.wireOp",EDGE,"E5"),sQuery(id+"F0.wireOp",EDGE,"E6"),subQ0,sQuery(id+"F0.wireOp",EDGE,"E8"),sQuery(id+"F0.wireOp",EDGE,"E9"),sQuery(id+"F0.wireOp",EDGE,"E10"),sQuery(id+"F0.wireOp",EDGE,"E11.MirrorCS"),sQuery(id+"F0.wireOp",EDGE,"E12.MirrorCS"),sQuery(id+"F0.wireOp",EDGE,"E13.MirrorCS"),sQuery(id+"F0.wireOp",EDGE,"E14.MirrorCS"),sQuery(id+"F0.wireOp",EDGE,"E15.MirrorCS"),sQuery(id+"F0.wireOp",EDGE,"E16.MirrorCS"),sQuery(id+"F0.wireOp",EDGE,"E17.MirrorCS"),sQuery(id+"F0.wireOp",EDGE,"E18.MirrorCS"),sQuery(id+"F0.wireOp",EDGE,"E19"),sQuery(id+"F0.wireOp",EDGE,"E20.MirrorCS"),sQuery(id+"F0.wireOp",EDGE,"E21"),sQuery(id+"F0.wireOp",EDGE,"E22.MirrorCS")])],"isStart":true})]});}
            var Q1;
            {var subQ0=sQuery(id+"F0.wireOp",EDGE,"E12.MirrorCS");Q1=makeQuery(id+"F10.opChamfer","BLEND_EDGE",EDGE,{"blendedFrom":[makeQuery(id+"F1.opExtrude","CAP_EDGE",EDGE,{"disambiguationData":[OSD([subQ0])],"isStart":true}),makeQuery(id+"F1.opExtrude","CAP_FACE",FACE,{"disambiguationData":[OSD([sQuery(id+"F0.wireOp",EDGE,"E0"),sQuery(id+"F0.wireOp",EDGE,"E1"),sQuery(id+"F0.wireOp",EDGE,"E4"),sQuery(id+"F0.wireOp",EDGE,"E5"),sQuery(id+"F0.wireOp",EDGE,"E6"),sQuery(id+"F0.wireOp",EDGE,"E7"),sQuery(id+"F0.wireOp",EDGE,"E8"),sQuery(id+"F0.wireOp",EDGE,"E9"),sQuery(id+"F0.wireOp",EDGE,"E10"),sQuery(id+"F0.wireOp",EDGE,"E11.MirrorCS"),subQ0,sQuery(id+"F0.wireOp",EDGE,"E13.MirrorCS"),sQuery(id+"F0.wireOp",EDGE,"E14.MirrorCS"),sQuery(id+"F0.wireOp",EDGE,"E15.MirrorCS"),sQuery(id+"F0.wireOp",EDGE,"E16.MirrorCS"),sQuery(id+"F0.wireOp",EDGE,"E17.MirrorCS"),sQuery(id+"F0.wireOp",EDGE,"E18.MirrorCS"),sQuery(id+"F0.wireOp",EDGE,"E19"),sQuery(id+"F0.wireOp",EDGE,"E20.MirrorCS"),sQuery(id+"F0.wireOp",EDGE,"E21"),sQuery(id+"F0.wireOp",EDGE,"E22.MirrorCS")])],"isStart":true})],"blendedInto":[makeQuery(id+"F1.opExtrude","CAP_FACE",FACE,{"disambiguationData":[OSD([sQuery(id+"F0.wireOp",EDGE,"E0"),sQuery(id+"F0.wireOp",EDGE,"E1"),sQuery(id+"F0.wireOp",EDGE,"E4"),sQuery(id+"F0.wireOp",EDGE,"E5"),sQuery(id+"F0.wireOp",EDGE,"E6"),sQuery(id+"F0.wireOp",EDGE,"E7"),sQuery(id+"F0.wireOp",EDGE,"E8"),sQuery(id+"F0.wireOp",EDGE,"E9"),sQuery(id+"F0.wireOp",EDGE,"E10"),sQuery(id+"F0.wireOp",EDGE,"E11.MirrorCS"),subQ0,sQuery(id+"F0.wireOp",EDGE,"E13.MirrorCS"),sQuery(id+"F0.wireOp",EDGE,"E14.MirrorCS"),sQuery(id+"F0.wireOp",EDGE,"E15.MirrorCS"),sQuery(id+"F0.wireOp",EDGE,"E16.MirrorCS"),sQuery(id+"F0.wireOp",EDGE,"E17.MirrorCS"),sQuery(id+"F0.wireOp",EDGE,"E18.MirrorCS"),sQuery(id+"F0.wireOp",EDGE,"E19"),sQuery(id+"F0.wireOp",EDGE,"E20.MirrorCS"),sQuery(id+"F0.wireOp",EDGE,"E21"),sQuery(id+"F0.wireOp",EDGE,"E22.MirrorCS")])],"isStart":true})]});}
            var Q2;
            {var subQ0=sQuery(id+"F0.wireOp",EDGE,"E7");Q2=makeQuery(id+"F11.opChamfer","BLEND_EDGE",EDGE,{"blendedFrom":[makeQuery(id+"F1.opExtrude","CAP_EDGE",EDGE,{"disambiguationData":[OSD([subQ0])],"isStart":false}),makeQuery(id+"F1.opExtrude","CAP_FACE",FACE,{"disambiguationData":[OSD([sQuery(id+"F0.wireOp",EDGE,"E0"),sQuery(id+"F0.wireOp",EDGE,"E1"),sQuery(id+"F0.wireOp",EDGE,"E4"),sQuery(id+"F0.wireOp",EDGE,"E5"),sQuery(id+"F0.wireOp",EDGE,"E6"),subQ0,sQuery(id+"F0.wireOp",EDGE,"E8"),sQuery(id+"F0.wireOp",EDGE,"E9"),sQuery(id+"F0.wireOp",EDGE,"E10"),sQuery(id+"F0.wireOp",EDGE,"E11.MirrorCS"),sQuery(id+"F0.wireOp",EDGE,"E12.MirrorCS"),sQuery(id+"F0.wireOp",EDGE,"E13.MirrorCS"),sQuery(id+"F0.wireOp",EDGE,"E14.MirrorCS"),sQuery(id+"F0.wireOp",EDGE,"E15.MirrorCS"),sQuery(id+"F0.wireOp",EDGE,"E16.MirrorCS"),sQuery(id+"F0.wireOp",EDGE,"E17.MirrorCS"),sQuery(id+"F0.wireOp",EDGE,"E18.MirrorCS"),sQuery(id+"F0.wireOp",EDGE,"E19"),sQuery(id+"F0.wireOp",EDGE,"E20.MirrorCS"),sQuery(id+"F0.wireOp",EDGE,"E21"),sQuery(id+"F0.wireOp",EDGE,"E22.MirrorCS")])],"isStart":false})],"blendedInto":[makeQuery(id+"F1.opExtrude","CAP_FACE",FACE,{"disambiguationData":[OSD([sQuery(id+"F0.wireOp",EDGE,"E0"),sQuery(id+"F0.wireOp",EDGE,"E1"),sQuery(id+"F0.wireOp",EDGE,"E4"),sQuery(id+"F0.wireOp",EDGE,"E5"),sQuery(id+"F0.wireOp",EDGE,"E6"),subQ0,sQuery(id+"F0.wireOp",EDGE,"E8"),sQuery(id+"F0.wireOp",EDGE,"E9"),sQuery(id+"F0.wireOp",EDGE,"E10"),sQuery(id+"F0.wireOp",EDGE,"E11.MirrorCS"),sQuery(id+"F0.wireOp",EDGE,"E12.MirrorCS"),sQuery(id+"F0.wireOp",EDGE,"E13.MirrorCS"),sQuery(id+"F0.wireOp",EDGE,"E14.MirrorCS"),sQuery(id+"F0.wireOp",EDGE,"E15.MirrorCS"),sQuery(id+"F0.wireOp",EDGE,"E16.MirrorCS"),sQuery(id+"F0.wireOp",EDGE,"E17.MirrorCS"),sQuery(id+"F0.wireOp",EDGE,"E18.MirrorCS"),sQuery(id+"F0.wireOp",EDGE,"E19"),sQuery(id+"F0.wireOp",EDGE,"E20.MirrorCS"),sQuery(id+"F0.wireOp",EDGE,"E21"),sQuery(id+"F0.wireOp",EDGE,"E22.MirrorCS")])],"isStart":false})]});}
            var Q3;
            {var subQ0=sQuery(id+"F0.wireOp",EDGE,"E12.MirrorCS");Q3=makeQuery(id+"F10.opChamfer","BLEND_EDGE",EDGE,{"blendedFrom":[makeQuery(id+"F1.opExtrude","CAP_EDGE",EDGE,{"disambiguationData":[OSD([subQ0])],"isStart":false}),makeQuery(id+"F1.opExtrude","CAP_FACE",FACE,{"disambiguationData":[OSD([sQuery(id+"F0.wireOp",EDGE,"E0"),sQuery(id+"F0.wireOp",EDGE,"E1"),sQuery(id+"F0.wireOp",EDGE,"E4"),sQuery(id+"F0.wireOp",EDGE,"E5"),sQuery(id+"F0.wireOp",EDGE,"E6"),sQuery(id+"F0.wireOp",EDGE,"E7"),sQuery(id+"F0.wireOp",EDGE,"E8"),sQuery(id+"F0.wireOp",EDGE,"E9"),sQuery(id+"F0.wireOp",EDGE,"E10"),sQuery(id+"F0.wireOp",EDGE,"E11.MirrorCS"),subQ0,sQuery(id+"F0.wireOp",EDGE,"E13.MirrorCS"),sQuery(id+"F0.wireOp",EDGE,"E14.MirrorCS"),sQuery(id+"F0.wireOp",EDGE,"E15.MirrorCS"),sQuery(id+"F0.wireOp",EDGE,"E16.MirrorCS"),sQuery(id+"F0.wireOp",EDGE,"E17.MirrorCS"),sQuery(id+"F0.wireOp",EDGE,"E18.MirrorCS"),sQuery(id+"F0.wireOp",EDGE,"E19"),sQuery(id+"F0.wireOp",EDGE,"E20.MirrorCS"),sQuery(id+"F0.wireOp",EDGE,"E21"),sQuery(id+"F0.wireOp",EDGE,"E22.MirrorCS")])],"isStart":false})],"blendedInto":[makeQuery(id+"F1.opExtrude","CAP_FACE",FACE,{"disambiguationData":[OSD([sQuery(id+"F0.wireOp",EDGE,"E0"),sQuery(id+"F0.wireOp",EDGE,"E1"),sQuery(id+"F0.wireOp",EDGE,"E4"),sQuery(id+"F0.wireOp",EDGE,"E5"),sQuery(id+"F0.wireOp",EDGE,"E6"),sQuery(id+"F0.wireOp",EDGE,"E7"),sQuery(id+"F0.wireOp",EDGE,"E8"),sQuery(id+"F0.wireOp",EDGE,"E9"),sQuery(id+"F0.wireOp",EDGE,"E10"),sQuery(id+"F0.wireOp",EDGE,"E11.MirrorCS"),subQ0,sQuery(id+"F0.wireOp",EDGE,"E13.MirrorCS"),sQuery(id+"F0.wireOp",EDGE,"E14.MirrorCS"),sQuery(id+"F0.wireOp",EDGE,"E15.MirrorCS"),sQuery(id+"F0.wireOp",EDGE,"E16.MirrorCS"),sQuery(id+"F0.wireOp",EDGE,"E17.MirrorCS"),sQuery(id+"F0.wireOp",EDGE,"E18.MirrorCS"),sQuery(id+"F0.wireOp",EDGE,"E19"),sQuery(id+"F0.wireOp",EDGE,"E20.MirrorCS"),sQuery(id+"F0.wireOp",EDGE,"E21"),sQuery(id+"F0.wireOp",EDGE,"E22.MirrorCS")])],"isStart":false})]});}
            chamfer(context, id + "F12", {"entities" : qUnion([Q0, Q1, Q2, Q3]), "width" : 3.5 * mm, "tangentPropagation" : true});
        }
    });
